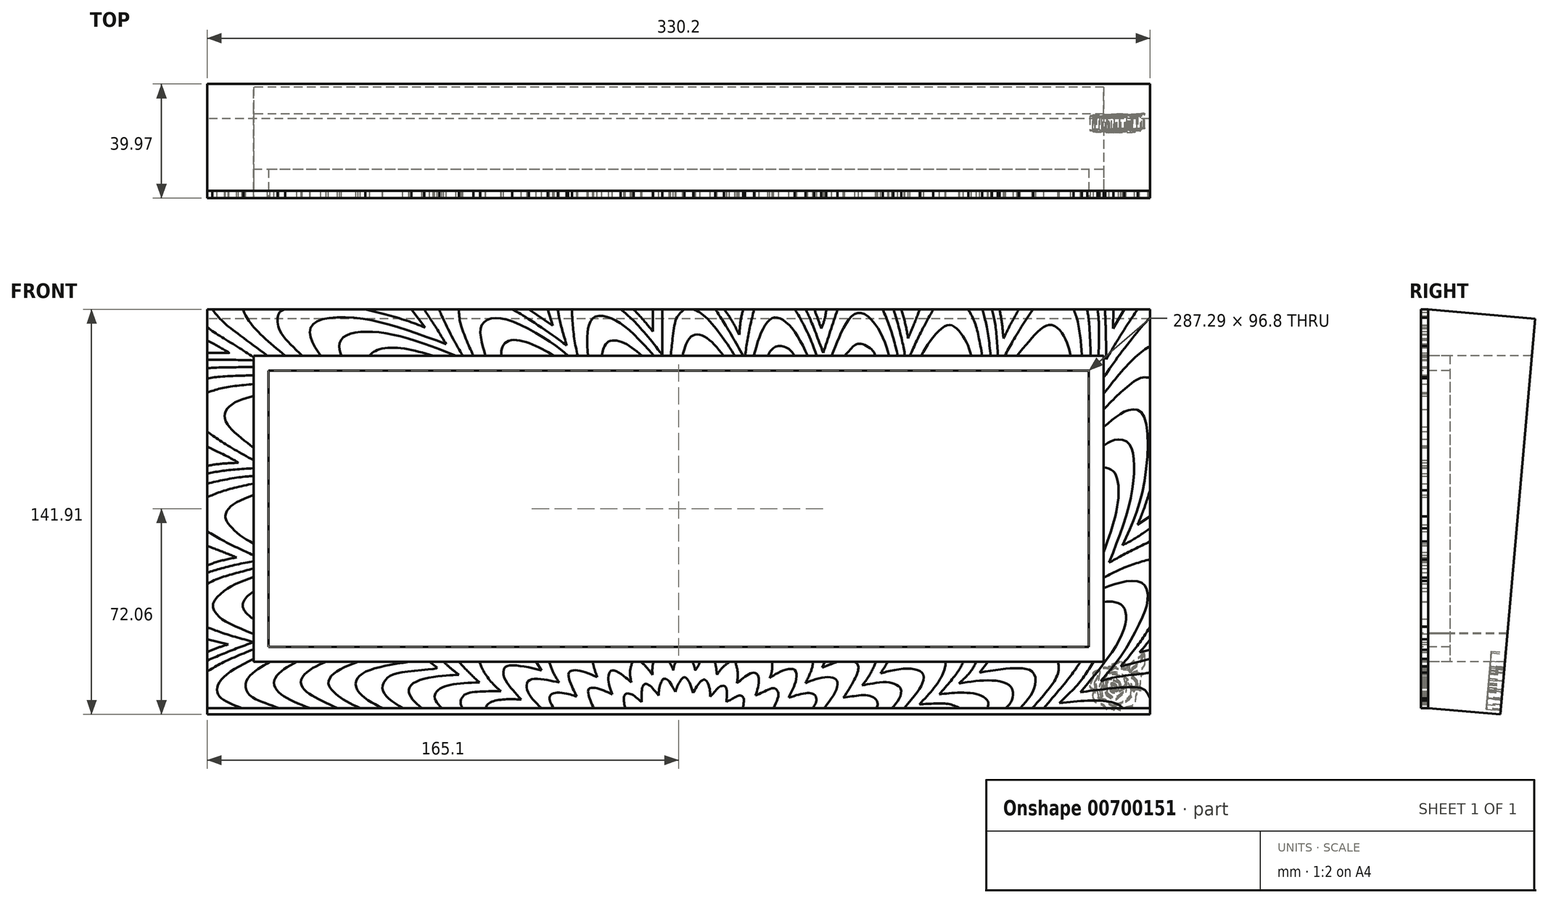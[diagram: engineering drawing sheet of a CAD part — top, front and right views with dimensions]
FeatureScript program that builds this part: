
annotation { "Feature Type Name" : "Feature", "Feature Type Description" : "" }
export const myFeature = defineFeature(function(context is Context, id is Id, definition is map)
    precondition{}
    {
        {
            var Q0;
            Q0=qCreatedBy(makeId("Front.planeOp"),FACE);
            var sketch = newSketch(context, id + "F0", { "sketchPlane" : qUnion([Q0])});
            skLineSegment(sketch, "E0.bottom", {"start": v(-143.64, 48.4) * mm, "end": v(143.64, 48.4) * mm});
            skLineSegment(sketch, "E0.top", {"start": v(-143.64, -48.4) * mm, "end": v(143.64, -48.4) * mm});
            skLineSegment(sketch, "E0.left", {"start": v(-143.64, 48.4) * mm, "end": v(-143.64, -48.4) * mm});
            skLineSegment(sketch, "E0.right", {"start": v(143.64, 48.4) * mm, "end": v(143.64, -48.4) * mm});
            skPoint(sketch, "E0.middle", {"position": v(0, 0) * mm});
            skLineSegment(sketch, "E1.bottom", {"start": v(-148.88, 53.63) * mm, "end": v(148.88, 53.63) * mm});
            skLineSegment(sketch, "E1.top", {"start": v(-148.88, -53.63) * mm, "end": v(148.88, -53.63) * mm});
            skLineSegment(sketch, "E1.left", {"start": v(-148.88, 53.63) * mm, "end": v(-148.88, -53.63) * mm});
            skLineSegment(sketch, "E1.right", {"start": v(148.88, 53.63) * mm, "end": v(148.88, -53.63) * mm});
            skLineSegment(sketch, "E2.bottom", {"start": v(-165.1, 69.85) * mm, "end": v(165.1, 69.85) * mm});
            skLineSegment(sketch, "E2.top", {"start": v(-165.1, -69.85) * mm, "end": v(165.1, -69.85) * mm});
            skLineSegment(sketch, "E2.left", {"start": v(-165.1, 69.85) * mm, "end": v(-165.1, -69.85) * mm});
            skLineSegment(sketch, "E2.right", {"start": v(165.1, 69.85) * mm, "end": v(165.1, -69.85) * mm});
            skFitSpline(sketch, "E3", {"points": [v(-148.88, -23.84) * mm, v(-155.66, -26.64) * mm, v(-160.5, -29.85) * mm, v(-163.16, -33.94) * mm, v(-161.11, -37.69) * mm, v(-156.13, -40.76) * mm, v(-148.88, -43.76) * mm, v(-148.88, -43.62) * mm], "startDerivative": vector(-39.33, -14.78) * mm, "endDerivative": vector(-2.7, 6.96) * mm});
            skFitSpline(sketch, "E4", {"points": [v(-148.88, -38.64) * mm, v(-150.68, -37.28) * mm, v(-152.18, -35.5) * mm, v(-152.66, -33.46) * mm, v(-151.36, -31) * mm, v(-148.88, -28.96) * mm], "startDerivative": vector(-9.73, 6.78) * mm, "endDerivative": vector(11.74, 8.3) * mm});
            skFitSpline(sketch, "E5", {"points": [v(-165.1, -26.23) * mm, v(-160.64, -24.25) * mm, v(-155.04, -22.55) * mm, v(-148.88, -20.91) * mm], "startDerivative": vector(13.98, 6.72) * mm, "endDerivative": vector(17.57, 4.62) * mm});
            skFitSpline(sketch, "E6", {"points": [v(-165.1, -22.41) * mm, v(-160.77, -21.05) * mm, v(-154.77, -19.55) * mm, v(-148.88, -18.39) * mm], "startDerivative": vector(13.7, 4.53) * mm, "endDerivative": vector(16.8, 3.12) * mm});
            skFitSpline(sketch, "E7", {"points": [v(-165.1, -19.82) * mm, v(-160.9, -18.39) * mm, v(-154.84, -17.03) * mm], "startDerivative": vector(8.7, 3.27) * mm, "endDerivative": vector(11.74, 2.35) * mm});
            skFitSpline(sketch, "E8", {"points": [v(-154.84, -17.03) * mm, v(-160.09, -14.91) * mm, v(-165.1, -13) * mm], "startDerivative": vector(-10.41, 4.25) * mm, "endDerivative": vector(-10.1, 3.8) * mm});
            skFitSpline(sketch, "E9", {"points": [v(-148.88, -16.28) * mm, v(-154.16, -13.82) * mm, v(-160.43, -10.68) * mm, v(-165.1, -7.96) * mm], "startDerivative": vector(-15.64, 7.2) * mm, "endDerivative": vector(-14.08, 8.56) * mm});
            skFitSpline(sketch, "E10", {"points": [v(-148.88, -12.18) * mm, v(-153.82, -9.12) * mm, v(-156.96, -6.11) * mm, v(-158.38, -4.14) * mm, v(-158.73, -2.7) * mm, v(-158.18, -0.73) * mm, v(-155.59, 1.8) * mm, v(-148.88, 4.86) * mm], "startDerivative": vector(-28.84, 16.16) * mm, "endDerivative": vector(36.5, 14.37) * mm});
            skFitSpline(sketch, "E11", {"points": [v(-165.1, 4.05) * mm, v(-159.27, 6.3) * mm, v(-148.88, 8.82) * mm], "startDerivative": vector(12.4, 5.36) * mm, "endDerivative": vector(19.72, 4.24) * mm});
            skFitSpline(sketch, "E12", {"points": [v(-165.1, 8.82) * mm, v(-158.25, 10.32) * mm, v(-151.7, 11.27) * mm, v(-148.88, 11.48) * mm], "startDerivative": vector(17.44, 4.14) * mm, "endDerivative": vector(10.33, 0.54) * mm});
            skFitSpline(sketch, "E13", {"points": [v(-165.1, 12.37) * mm, v(-158.93, 13.39) * mm, v(-148.88, 14.2) * mm], "startDerivative": vector(13.13, 2.51) * mm, "endDerivative": vector(19.08, 1.22) * mm});
            skFitSpline(sketch, "E14", {"points": [v(-165.1, 15.1) * mm, v(-160.09, 15.77) * mm, v(-154.23, 16.12) * mm], "startDerivative": vector(10.2, 1.6) * mm, "endDerivative": vector(11.54, 0.46) * mm});
            skFitSpline(sketch, "E15", {"points": [v(-165.1, 21.78) * mm, v(-161.73, 20.14) * mm, v(-156.4, 17.48) * mm, v(-154.23, 16.12) * mm], "startDerivative": vector(9.43, -4.6) * mm, "endDerivative": vector(6.91, -4.68) * mm});
            skFitSpline(sketch, "E16", {"points": [v(-165.1, 27.1) * mm, v(-161.73, 24.64) * mm, v(-156.27, 21.16) * mm, v(-148.88, 17) * mm], "startDerivative": vector(11.67, -8.74) * mm, "endDerivative": vector(19.59, -10.74) * mm});
            skFitSpline(sketch, "E17", {"points": [v(-148.88, 21.37) * mm, v(-153.68, 25.19) * mm, v(-157.9, 29.41) * mm, v(-159, 32.48) * mm, v(-158.25, 34.87) * mm, v(-154.43, 37.73) * mm, v(-148.88, 39.44) * mm], "startDerivative": vector(-24.8, 19.26) * mm, "endDerivative": vector(30.57, 7.1) * mm});
            skFitSpline(sketch, "E18", {"points": [v(-165.1, 40.73) * mm, v(-159.07, 42.44) * mm, v(-148.88, 43.67) * mm], "startDerivative": vector(12.79, 4.26) * mm, "endDerivative": vector(19.4, 1.7) * mm});
            skFitSpline(sketch, "E19", {"points": [v(-165.1, 45.64) * mm, v(-160.02, 46.32) * mm, v(-151.97, 46.67) * mm, v(-148.88, 46.8) * mm], "startDerivative": vector(13.86, 2.35) * mm, "endDerivative": vector(10.3, 0.54) * mm});
            skFitSpline(sketch, "E20", {"points": [v(-165.1, 49.26) * mm, v(-161.52, 49.46) * mm, v(-153.48, 49.6) * mm, v(-148.88, 49.6) * mm], "startDerivative": vector(11.27, 0.81) * mm, "endDerivative": vector(13.17, -0.05) * mm});
            skFitSpline(sketch, "E21", {"points": [v(-165.1, 52.19) * mm, v(-158.25, 52.19) * mm, v(-148.88, 51.98) * mm], "startDerivative": vector(14.29, 0.09) * mm, "endDerivative": vector(18.06, -0.48) * mm});
            skFitSpline(sketch, "E22", {"points": [v(-148.88, 53.08) * mm, v(-154.43, 56.69) * mm, v(-160.7, 60.58) * mm, v(-165.1, 63.5) * mm], "startDerivative": vector(-15.86, 10.52) * mm, "endDerivative": vector(-13.7, 9.38) * mm});
            skFitSpline(sketch, "E23", {"points": [v(-165.1, 59) * mm, v(-157.43, 54.58) * mm, v(-157.57, 54.58) * mm], "startDerivative": vector(13, -7.2) * mm, "endDerivative": vector(-1.78, 0.27) * mm});
            skFitSpline(sketch, "E24", {"points": [v(-157.43, 54.58) * mm, v(-165.1, 54.58) * mm], "startDerivative": vector(-7.67, 0) * mm, "endDerivative": vector(-7.67, 0) * mm});
            skFitSpline(sketch, "E25", {"points": [v(-163.36, 69.85) * mm, v(-159.89, 65.83) * mm, v(-155.45, 62.15) * mm, v(-144.06, 53.63) * mm], "startDerivative": vector(12.55, -15.56) * mm, "endDerivative": vector(28.56, -21.28) * mm});
            skFitSpline(sketch, "E26", {"points": [v(-152.45, 69.85) * mm, v(-151.9, 68.15) * mm, v(-148.22, 62.96) * mm, v(-137.8, 53.63) * mm], "startDerivative": vector(2, -8.7) * mm, "endDerivative": vector(23.58, -19.42) * mm});
            skFitSpline(sketch, "E27", {"points": [v(-137.8, 69.85) * mm, v(-139.63, 68.96) * mm, v(-140.45, 66.78) * mm, v(-139.7, 62.49) * mm, v(-131.86, 53.63) * mm], "startDerivative": vector(-12.3, -3.75) * mm, "endDerivative": vector(24.12, -22.95) * mm});
            skFitSpline(sketch, "E28", {"points": [v(-125.31, 53.63) * mm, v(-127.84, 57.5) * mm, v(-129.2, 61.94) * mm, v(-128.04, 64.67) * mm, v(-122.93, 66.78) * mm, v(-111.06, 66.58) * mm, v(-97.97, 63.5) * mm, v(-81.46, 57.71) * mm], "startDerivative": vector(-24.33, 33.6) * mm, "endDerivative": vector(79.98, -29.52) * mm});
            skFitSpline(sketch, "E29", {"points": [v(-89.17, 69.85) * mm, v(-85.42, 64.2) * mm, v(-81.46, 57.71) * mm], "startDerivative": vector(7.72, -11.4) * mm, "endDerivative": vector(7.7, -12.85) * mm});
            skFitSpline(sketch, "E30", {"points": [v(-109.76, 69.85) * mm, v(-97.63, 66.65) * mm, v(-88.76, 63.5) * mm], "startDerivative": vector(23.6, -5.77) * mm, "endDerivative": vector(18.29, -6.94) * mm});
            skFitSpline(sketch, "E31", {"points": [v(-88.76, 63.5) * mm, v(-93.6, 69.85) * mm], "startDerivative": vector(-4.84, 6.34) * mm, "endDerivative": vector(-4.84, 6.34) * mm});
            skFitSpline(sketch, "E32", {"points": [v(-118.15, 53.63) * mm, v(-118.9, 56.76) * mm, v(-117.67, 59.83) * mm, v(-111.95, 61.87) * mm, v(-98.72, 60.71) * mm, v(-77.99, 53.63) * mm], "startDerivative": vector(-8.96, 24.79) * mm, "endDerivative": vector(66.04, -25.79) * mm});
            skFitSpline(sketch, "E33", {"points": [v(-108.2, 53.63) * mm, v(-107.38, 54.58) * mm, v(-104.24, 56) * mm, v(-96.47, 56.14) * mm, v(-85.97, 53.63) * mm], "startDerivative": vector(5.26, 7.61) * mm, "endDerivative": vector(29.33, -8.5) * mm});
            skFitSpline(sketch, "E34", {"points": [v(-75.6, 53.63) * mm, v(-79.35, 60.24) * mm, v(-82.83, 67.33) * mm, v(-83.85, 69.85) * mm], "startDerivative": vector(-9.68, 16.45) * mm, "endDerivative": vector(-3.62, 9.55) * mm});
            skFitSpline(sketch, "E35", {"points": [v(-71.92, 53.63) * mm, v(-74.65, 59.9) * mm, v(-76.62, 65.9) * mm, v(-76.96, 69.85) * mm], "startDerivative": vector(-7.6, 16.87) * mm, "endDerivative": vector(-0.28, 13.46) * mm});
            skFitSpline(sketch, "E36", {"points": [v(-67.7, 53.63) * mm, v(-68.92, 58.33) * mm, v(-69.4, 62.76) * mm, v(-68.03, 65.49) * mm, v(-64.55, 66.78) * mm, v(-56.92, 65.08) * mm, v(-43.82, 57.71) * mm, v(-38.78, 53.63) * mm], "startDerivative": vector(-10.07, 36.36) * mm, "endDerivative": vector(28.31, -25.37) * mm});
            skFitSpline(sketch, "E37", {"points": [v(-62.17, 53.63) * mm, v(-61.83, 56.42) * mm, v(-60.05, 58.6) * mm, v(-56.03, 59) * mm, v(-49.82, 56.96) * mm, v(-43.62, 53.63) * mm], "startDerivative": vector(0.32, 18.02) * mm, "endDerivative": vector(24.27, -14) * mm});
            skFitSpline(sketch, "E38", {"points": [v(-58.28, 69.85) * mm, v(-53.03, 66.78) * mm, v(-39.19, 57.1) * mm, v(-39.32, 57.1) * mm], "startDerivative": vector(10.3, -5.3) * mm, "endDerivative": vector(-3.94, 0.9) * mm});
            skFitSpline(sketch, "E39", {"points": [v(-52.48, 69.85) * mm, v(-44.1, 64.12) * mm], "startDerivative": vector(8.39, -5.73) * mm, "endDerivative": vector(8.39, -5.73) * mm});
            skFitSpline(sketch, "E40", {"points": [v(-44.1, 64.12) * mm, v(-45.87, 69.85) * mm], "startDerivative": vector(-1.77, 5.73) * mm, "endDerivative": vector(-1.77, 5.73) * mm});
            skFitSpline(sketch, "E41", {"points": [v(-42.32, 69.85) * mm, v(-41.7, 66.24) * mm, v(-39.19, 57.1) * mm], "startDerivative": vector(1.12, -8.4) * mm, "endDerivative": vector(4.86, -16.48) * mm});
            skFitSpline(sketch, "E42", {"points": [v(-35.37, 53.63) * mm, v(-36.6, 59.9) * mm, v(-37.2, 66.24) * mm, v(-37.41, 69.85) * mm], "startDerivative": vector(-3.76, 16.86) * mm, "endDerivative": vector(-0.63, 12.2) * mm});
            skFitSpline(sketch, "E43", {"points": [v(-31.75, 53.63) * mm, v(-32.03, 59.9) * mm, v(-31.28, 64.67) * mm, v(-29.23, 67.33) * mm, v(-24.6, 67.05) * mm, v(-18.39, 63.5) * mm, v(-8.7, 53.63) * mm], "startDerivative": vector(-2.92, 38.7) * mm, "endDerivative": vector(40.7, -45.2) * mm});
            skFitSpline(sketch, "E44", {"points": [v(-26.91, 53.63) * mm, v(-26.37, 56.14) * mm, v(-24.53, 58.53) * mm, v(-19.96, 58.46) * mm, v(-12.8, 53.63) * mm], "startDerivative": vector(1.83, 13.08) * mm, "endDerivative": vector(20.6, -17.01) * mm});
            skFitSpline(sketch, "E45", {"points": [v(-20.3, 69.85) * mm, v(-15.05, 65.15) * mm, v(-5.74, 53.97) * mm], "startDerivative": vector(12.18, -9.92) * mm, "endDerivative": vector(16.67, -21.17) * mm});
            skFitSpline(sketch, "E46", {"points": [v(-5.74, 53.97) * mm, v(-5.74, 60.07) * mm, v(-5.74, 67.58) * mm, v(-5.74, 69.85) * mm], "startDerivative": vector(0, 15.42) * mm, "endDerivative": vector(0, 8.42) * mm});
            skFitSpline(sketch, "E47", {"points": [v(-15.8, 69.85) * mm, v(-12.11, 65.88) * mm, v(-9.05, 62.06) * mm], "startDerivative": vector(7.41, -7.73) * mm, "endDerivative": vector(6.08, -7.85) * mm});
            skFitSpline(sketch, "E48", {"points": [v(-9.05, 62.06) * mm, v(-9.05, 69.85) * mm], "startDerivative": vector(0, 7.8) * mm, "endDerivative": vector(0, 7.8) * mm});
            skFitSpline(sketch, "E49", {"points": [v(-2.77, 53.63) * mm, v(-2.16, 59.4) * mm, v(-0.66, 66.9) * mm, v(2, 69.85) * mm], "startDerivative": vector(1.72, 15.96) * mm, "endDerivative": vector(10.73, 8.47) * mm});
            skFitSpline(sketch, "E50", {"points": [v(5.14, 69.85) * mm, v(8.34, 68.13) * mm, v(15.1, 60.42) * mm, v(19.66, 53.63) * mm], "startDerivative": vector(12.47, -4.75) * mm, "endDerivative": vector(11.4, -17.9) * mm});
            skFitSpline(sketch, "E51", {"points": [v(1.39, 53.63) * mm, v(2.55, 57.56) * mm, v(5.14, 60.76) * mm, v(9.43, 60.08) * mm, v(15.78, 53.63) * mm], "startDerivative": vector(4.01, 17.68) * mm, "endDerivative": vector(18.96, -23.43) * mm});
            skFitSpline(sketch, "E52", {"points": [v(12.84, 69.85) * mm, v(16.46, 64.24) * mm, v(22.6, 53.63) * mm], "startDerivative": vector(8.06, -12.1) * mm, "endDerivative": vector(11.28, -19.95) * mm});
            skFitSpline(sketch, "E53", {"points": [v(15.84, 69.85) * mm, v(18.03, 66.9) * mm, v(21.23, 60.97) * mm], "startDerivative": vector(5.05, -6.24) * mm, "endDerivative": vector(5.7, -11.28) * mm});
            skFitSpline(sketch, "E54", {"points": [v(21.23, 60.97) * mm, v(21.78, 66.22) * mm, v(22.6, 69.85) * mm], "startDerivative": vector(0.79, 10.12) * mm, "endDerivative": vector(1.97, 7.57) * mm});
            skFitSpline(sketch, "E55", {"points": [v(23.25, 53.63) * mm, v(24.5, 61.49) * mm, v(26.41, 69.85) * mm], "startDerivative": vector(2.24, 15.93) * mm, "endDerivative": vector(4.07, 16.52) * mm});
            skFitSpline(sketch, "E56", {"points": [v(26.35, 53.63) * mm, v(28.6, 60.97) * mm, v(31.4, 65.74) * mm, v(33.78, 67.04) * mm, v(36.5, 66.15) * mm, v(40.6, 62.06) * mm, v(45.23, 53.63) * mm], "startDerivative": vector(10.1, 38.33) * mm, "endDerivative": vector(19.94, -41.1) * mm});
            skFitSpline(sketch, "E57", {"points": [v(31.19, 53.63) * mm, v(33.03, 56.2) * mm, v(35.48, 57.08) * mm, v(38.69, 55.85) * mm, v(40.6, 53.63) * mm], "startDerivative": vector(6.45, 11.28) * mm, "endDerivative": vector(6.6, -9.69) * mm});
            skFitSpline(sketch, "E58", {"points": [v(40.67, 69.85) * mm, v(42.64, 66.63) * mm, v(46.33, 58.99) * mm, v(48.37, 53.63) * mm], "startDerivative": vector(6.8, -10.33) * mm, "endDerivative": vector(5.33, -15.03) * mm});
            skFitSpline(sketch, "E59", {"points": [v(44.48, 69.85) * mm, v(46.33, 65.8) * mm, v(50.62, 54.62) * mm], "startDerivative": vector(4.48, -9.3) * mm, "endDerivative": vector(7.55, -20.27) * mm});
            skFitSpline(sketch, "E60", {"points": [v(50.62, 54.62) * mm, v(53.08, 62.06) * mm, v(55.67, 69.85) * mm], "startDerivative": vector(4.93, 14.96) * mm, "endDerivative": vector(5.16, 15.5) * mm});
            skFitSpline(sketch, "E61", {"points": [v(47.49, 69.85) * mm, v(48.71, 66.63) * mm, v(49.94, 63.08) * mm], "startDerivative": vector(2.53, -6.5) * mm, "endDerivative": vector(2.38, -7.04) * mm});
            skFitSpline(sketch, "E62", {"points": [v(49.94, 63.08) * mm, v(51.17, 66.63) * mm, v(51.71, 69.85) * mm], "startDerivative": vector(2.7, 6.9) * mm, "endDerivative": vector(0.83, 6.63) * mm});
            skFitSpline(sketch, "E63", {"points": [v(53.55, 53.63) * mm, v(56.28, 60.22) * mm, v(59.83, 66.63) * mm, v(63.1, 68.68) * mm, v(67.2, 66.63) * mm, v(71.56, 59.94) * mm, v(73.67, 53.63) * mm], "startDerivative": vector(14.4, 36.04) * mm, "endDerivative": vector(9.88, -35.67) * mm});
            skFitSpline(sketch, "E64", {"points": [v(58.2, 53.63) * mm, v(61.26, 56.94) * mm, v(63.51, 57.83) * mm, v(67.53, 55.85) * mm, v(68.9, 53.63) * mm], "startDerivative": vector(11.09, 13.09) * mm, "endDerivative": vector(4.16, -10.31) * mm});
            skFitSpline(sketch, "E65", {"points": [v(71.49, 69.85) * mm, v(74.49, 62.06) * mm, v(76.74, 53.63) * mm], "startDerivative": vector(6.47, -15.53) * mm, "endDerivative": vector(4.04, -16.91) * mm});
            skFitSpline(sketch, "E66", {"points": [v(75.17, 69.85) * mm, v(76.53, 65.67) * mm, v(78.38, 58.3) * mm, v(79.26, 53.63) * mm], "startDerivative": vector(4.43, -12.65) * mm, "endDerivative": vector(2.4, -13.87) * mm});
            skFitSpline(sketch, "E67", {"points": [v(77.97, 69.85) * mm, v(79.33, 64.99) * mm, v(80.35, 59.67) * mm], "startDerivative": vector(2.96, -9.76) * mm, "endDerivative": vector(1.82, -10.6) * mm});
            skFitSpline(sketch, "E68", {"points": [v(80.35, 59.67) * mm, v(82.6, 65.13) * mm, v(84.44, 69.85) * mm], "startDerivative": vector(4.47, 10.7) * mm, "endDerivative": vector(3.7, 9.65) * mm});
            skFitSpline(sketch, "E69", {"points": [v(81.04, 53.63) * mm, v(84.38, 60.97) * mm, v(89.15, 69.85) * mm], "startDerivative": vector(6.61, 15.25) * mm, "endDerivative": vector(9.56, 17.17) * mm});
            skFitSpline(sketch, "E70", {"points": [v(85, 53.63) * mm, v(88.74, 59.67) * mm, v(93.17, 63.9) * mm, v(95.7, 64.24) * mm, v(98.36, 62.06) * mm, v(100.81, 58.3) * mm, v(102.52, 53.63) * mm], "startDerivative": vector(16.58, 30) * mm, "endDerivative": vector(8.73, -28.02) * mm});
            skFitSpline(sketch, "E71", {"points": [v(106.33, 69.85) * mm, v(107.7, 64.65) * mm, v(109.33, 53.63) * mm], "startDerivative": vector(3.44, -11.46) * mm, "endDerivative": vector(2.61, -20.45) * mm});
            skFitSpline(sketch, "E72", {"points": [v(109.68, 69.85) * mm, v(110.9, 64.44) * mm, v(111.79, 53.63) * mm], "startDerivative": vector(3.24, -11.8) * mm, "endDerivative": vector(1.1, -20.18) * mm});
            skFitSpline(sketch, "E73", {"points": [v(101.5, 69.85) * mm, v(103.47, 65.8) * mm, v(104.9, 60.97) * mm, v(106.33, 53.63) * mm], "startDerivative": vector(7.11, -13.3) * mm, "endDerivative": vector(3.64, -20.03) * mm});
            skFitSpline(sketch, "E74", {"points": [v(112.4, 69.85) * mm, v(113.15, 65.4) * mm, v(113.77, 59.67) * mm], "startDerivative": vector(1.7, -9.17) * mm, "endDerivative": vector(1.04, -11.15) * mm});
            skFitSpline(sketch, "E75", {"points": [v(113.77, 59.67) * mm, v(116.09, 64.3) * mm, v(119.09, 69.85) * mm], "startDerivative": vector(4.67, 9.55) * mm, "endDerivative": vector(5.94, 10.78) * mm});
            skFitSpline(sketch, "E76", {"points": [v(114.24, 53.63) * mm, v(118, 60.42) * mm, v(124.13, 69.85) * mm], "startDerivative": vector(7.6, 14.46) * mm, "endDerivative": vector(12.05, 17.89) * mm});
            skFitSpline(sketch, "E77", {"points": [v(118.47, 53.63) * mm, v(123.59, 59.67) * mm, v(127.88, 63.7) * mm, v(130.82, 64.3) * mm, v(133.88, 62.06) * mm, v(136.2, 57.62) * mm, v(137.23, 53.63) * mm], "startDerivative": vector(24.07, 29.06) * mm, "endDerivative": vector(5.32, -25.45) * mm});
            skFitSpline(sketch, "E78", {"points": [v(138.32, 69.85) * mm, v(139.48, 66.63) * mm, v(140.63, 60.28) * mm, v(141.25, 53.63) * mm], "startDerivative": vector(4.55, -10.98) * mm, "endDerivative": vector(1.33, -17.7) * mm});
            skFitSpline(sketch, "E79", {"points": [v(143.09, 69.85) * mm, v(143.7, 65.4) * mm, v(144.32, 53.63) * mm], "startDerivative": vector(1.73, -10.25) * mm, "endDerivative": vector(0.8, -21.32) * mm});
            skFitSpline(sketch, "E80", {"points": [v(146.7, 69.85) * mm, v(147.18, 64.65) * mm, v(147.04, 53.63) * mm], "startDerivative": vector(1.46, -11.56) * mm, "endDerivative": vector(-0.65, -20.34) * mm});
            skFitSpline(sketch, "E81", {"points": [v(149.3, 69.85) * mm, v(149.57, 63.08) * mm, v(149.77, 52.37) * mm], "startDerivative": vector(0.67, -14.4) * mm, "endDerivative": vector(0.3, -20.32) * mm});
            skFitSpline(sketch, "E82", {"points": [v(149.77, 52.37) * mm, v(155.57, 62.06) * mm, v(160.75, 69.85) * mm], "startDerivative": vector(11.13, 19.06) * mm, "endDerivative": vector(10.83, 15.84) * mm});
            skFitSpline(sketch, "E83", {"points": [v(152.16, 63.08) * mm, v(152.23, 69.85) * mm], "startDerivative": vector(0.07, 6.77) * mm, "endDerivative": vector(0.07, 6.77) * mm});
            skFitSpline(sketch, "E84", {"points": [v(152.16, 63.08) * mm, v(156.11, 69.85) * mm], "startDerivative": vector(3.96, 6.77) * mm, "endDerivative": vector(3.96, 6.77) * mm});
            skFitSpline(sketch, "E85", {"points": [v(148.88, 46.03) * mm, v(155.1, 54.9) * mm, v(162.66, 64.3) * mm, v(165.1, 66.97) * mm], "startDerivative": vector(15.04, 22.34) * mm, "endDerivative": vector(9.51, 9.94) * mm});
            skFitSpline(sketch, "E86", {"points": [v(148.88, 40.3) * mm, v(154.68, 47.53) * mm, v(161.43, 54.42) * mm, v(165.1, 57.01) * mm], "startDerivative": vector(14.89, 19.32) * mm, "endDerivative": vector(13.38, 8.38) * mm});
            skFitSpline(sketch, "E87", {"points": [v(148.88, 34.85) * mm, v(153.11, 39.15) * mm, v(157.48, 43.03) * mm, v(162.25, 45.96) * mm, v(165.1, 45.76) * mm], "startDerivative": vector(15.42, 15.98) * mm, "endDerivative": vector(14.28, -3.64) * mm});
            skFitSpline(sketch, "E88", {"points": [v(148.88, 28.72) * mm, v(153.89, 32.66) * mm, v(158.66, 34.8) * mm, v(162.72, 32.9) * mm, v(162.72, 7.48) * mm, v(155.44, -12.8) * mm], "startDerivative": vector(32.62, 27.37) * mm, "endDerivative": vector(-29.95, -63.67) * mm});
            skFitSpline(sketch, "E89", {"points": [v(155.44, -12.8) * mm, v(159.98, -10.3) * mm, v(165.1, -6.84) * mm], "startDerivative": vector(9.41, 4.91) * mm, "endDerivative": vector(9.9, 6.99) * mm});
            skFitSpline(sketch, "E90", {"points": [v(160.7, -5.65) * mm, v(165.1, -2.66) * mm], "startDerivative": vector(4.4, 2.98) * mm, "endDerivative": vector(4.4, 2.98) * mm});
            skFitSpline(sketch, "E91", {"points": [v(160.7, -5.65) * mm, v(162.96, 0) * mm, v(165.1, 6.52) * mm], "startDerivative": vector(4.8, 11.4) * mm, "endDerivative": vector(4.02, 12.93) * mm});
            skFitSpline(sketch, "E92", {"points": [v(150.8, -18.85) * mm, v(156.66, -15.65) * mm, v(165.1, -11.49) * mm], "startDerivative": vector(12.2, 6.86) * mm, "endDerivative": vector(16.3, 7.84) * mm});
            skFitSpline(sketch, "E93", {"points": [v(148.88, 14.47) * mm, v(151.98, 13.4) * mm, v(153.89, 8.86) * mm, v(153.3, -0.93) * mm, v(148.88, -15.25) * mm], "startDerivative": vector(20.66, -3.26) * mm, "endDerivative": vector(-14.87, -42) * mm});
            skFitSpline(sketch, "E94", {"points": [v(148.88, -24.07) * mm, v(157.48, -20.05) * mm, v(165.1, -17.73) * mm], "startDerivative": vector(16.62, 8.45) * mm, "endDerivative": vector(15.82, 4.17) * mm});
            skFitSpline(sketch, "E95", {"points": [v(148.88, -27.82) * mm, v(154.68, -25.84) * mm, v(160.7, -25.36) * mm, v(163.55, -27.34) * mm, v(164.23, -31.98) * mm, v(162.39, -38.05) * mm, v(155.44, -50.8) * mm, v(147.77, -60.35) * mm], "startDerivative": vector(42.5, 16.57) * mm, "endDerivative": vector(-41.64, -46.77) * mm});
            skFitSpline(sketch, "E96", {"points": [v(148.88, -32.67) * mm, v(151.95, -32.55) * mm, v(155.05, -33.62) * mm, v(156.6, -36.49) * mm, v(154.81, -44.96) * mm, v(140.73, -64.3) * mm], "startDerivative": vector(22.67, 2.49) * mm, "endDerivative": vector(-46.2, -55.37) * mm});
            skFitSpline(sketch, "E97", {"points": [v(140.73, -64.3) * mm, v(147.65, -63.34) * mm, v(157.44, -62.5) * mm, v(163.04, -63.34) * mm, v(165.1, -66.44) * mm], "startDerivative": vector(24.84, 3.68) * mm, "endDerivative": vector(8.15, -18.92) * mm});
            skFitSpline(sketch, "E98", {"points": [v(147.77, -60.35) * mm, v(153.5, -58.92) * mm, v(162.8, -57.73) * mm, v(165.1, -57.37) * mm], "startDerivative": vector(14.5, 4.39) * mm, "endDerivative": vector(8.35, 1.52) * mm});
            skFitSpline(sketch, "E99", {"points": [v(154.81, -55.22) * mm, v(161.37, -46.99) * mm, v(165.1, -41.26) * mm], "startDerivative": vector(12.82, 15.43) * mm, "endDerivative": vector(7.57, 12.39) * mm});
            skFitSpline(sketch, "E100", {"points": [v(154.81, -55.22) * mm, v(165.1, -52.6) * mm], "startDerivative": vector(10.29, 2.63) * mm, "endDerivative": vector(10.29, 2.63) * mm});
            skFitSpline(sketch, "E101", {"points": [v(161.37, -50.33) * mm, v(165.1, -45.68) * mm, v(165.1, -45.56) * mm], "startDerivative": vector(6.12, 7.22) * mm, "endDerivative": vector(-0.26, 0.7) * mm});
            skFitSpline(sketch, "E102", {"points": [v(161.37, -50.33) * mm, v(165.1, -49.38) * mm], "startDerivative": vector(3.73, 0.95) * mm, "endDerivative": vector(3.73, 0.95) * mm});
            skFitSpline(sketch, "E103", {"points": [v(133.33, -68.11) * mm, v(140.73, -60.35) * mm, v(145.26, -53.63) * mm], "startDerivative": vector(14.93, 14.52) * mm, "endDerivative": vector(8.8, 14.45) * mm});
            skFitSpline(sketch, "E104", {"points": [v(133.33, -68.11) * mm, v(145.5, -67.16) * mm, v(152.9, -68.11) * mm, v(155.65, -69.85) * mm], "startDerivative": vector(28.97, 3.25) * mm, "endDerivative": vector(10.49, -8.56) * mm});
            skFitSpline(sketch, "E105", {"points": [v(140.73, -53.63) * mm, v(137.27, -58.56) * mm, v(127.84, -69.85) * mm], "startDerivative": vector(-7.58, -11.5) * mm, "endDerivative": vector(-17.48, -20.3) * mm});
            skFitSpline(sketch, "E106", {"points": [v(132.81, -53.63) * mm, v(133.08, -54.75) * mm, v(132.81, -57.67) * mm, v(130.51, -61.88) * mm, v(123.85, -69.85) * mm], "startDerivative": vector(2.51, -7.5) * mm, "endDerivative": vector(-19, -21.7) * mm});
            skFitSpline(sketch, "E107", {"points": [v(119.68, -69.85) * mm, v(123.19, -65.54) * mm, v(124.98, -60.98) * mm, v(124, -57.2) * mm, v(120.3, -55.92) * mm, v(114.46, -56.07) * mm, v(105.42, -57.36) * mm], "startDerivative": vector(22.35, 24.78) * mm, "endDerivative": vector(-43.85, -6.97) * mm});
            skFitSpline(sketch, "E108", {"points": [v(105.42, -57.36) * mm, v(108.26, -53.63) * mm], "startDerivative": vector(2.84, 3.74) * mm, "endDerivative": vector(2.84, 3.74) * mm});
            skFitSpline(sketch, "E109", {"points": [v(114.6, -69.85) * mm, v(116.87, -66.57) * mm, v(116.27, -62.27) * mm, v(109, -60.12) * mm, v(98.13, -61.2) * mm], "startDerivative": vector(13.91, 14.94) * mm, "endDerivative": vector(-33.46, -5.33) * mm});
            skFitSpline(sketch, "E110", {"points": [v(98.13, -61.2) * mm, v(102.07, -57.26) * mm, v(104.22, -53.63) * mm], "startDerivative": vector(8.1, 7.25) * mm, "endDerivative": vector(3.98, 7.9) * mm});
            skFitSpline(sketch, "E111", {"points": [v(99.74, -53.63) * mm, v(97.7, -57.18) * mm, v(91.29, -65.02) * mm], "startDerivative": vector(-4.24, -8.42) * mm, "endDerivative": vector(-12.09, -13.96) * mm});
            skFitSpline(sketch, "E112", {"points": [v(91.29, -65.02) * mm, v(96.74, -64.48) * mm, v(104.72, -65.02) * mm, v(108.27, -67.34) * mm, v(108.2, -69.85) * mm], "startDerivative": vector(19.06, 2.44) * mm, "endDerivative": vector(-3.42, -14.51) * mm});
            skFitSpline(sketch, "E113", {"points": [v(-165.1, -41.5) * mm, v(-158.73, -43.82) * mm, v(-148.88, -46.69) * mm], "startDerivative": vector(13.4, -5.16) * mm, "endDerivative": vector(18.87, -5.2) * mm});
            skFitSpline(sketch, "E114", {"points": [v(-148.88, -46.69) * mm, v(-157.84, -50.1) * mm, v(-165.1, -53.17) * mm], "startDerivative": vector(-17.57, -6.51) * mm, "endDerivative": vector(-14.84, -6.44) * mm});
            skFitSpline(sketch, "E115", {"points": [v(-165.1, -50.17) * mm, v(-161.52, -48.73) * mm, v(-157.77, -47.5) * mm], "startDerivative": vector(7.14, 3) * mm, "endDerivative": vector(7.52, 2.33) * mm});
            skFitSpline(sketch, "E116", {"points": [v(-157.77, -47.5) * mm, v(-165.1, -45.67) * mm], "startDerivative": vector(-7.33, 1.84) * mm, "endDerivative": vector(-7.33, 1.84) * mm});
            skFitSpline(sketch, "E117", {"points": [v(-165.1, -57.02) * mm, v(-159.4, -53.75) * mm, v(-148.88, -49.25) * mm], "startDerivative": vector(12.07, 7.53) * mm, "endDerivative": vector(20.01, 8) * mm});
            skFitSpline(sketch, "E118", {"points": [v(-152.93, -69.85) * mm, v(-158.38, -67.52) * mm, v(-161.04, -65.4) * mm, v(-161.59, -62.68) * mm, v(-159.27, -58.86) * mm, v(-148.88, -52.52) * mm], "startDerivative": vector(-27.82, 10.81) * mm, "endDerivative": vector(40.24, 20.96) * mm});
            skFitSpline(sketch, "E119", {"points": [v(-143.08, -53.63) * mm, v(-148.2, -56.73) * mm, v(-151.47, -60.68) * mm, v(-150.72, -64.77) * mm, v(-145.67, -67.7) * mm, v(-140.01, -69.85) * mm], "startDerivative": vector(-25.14, -13.6) * mm, "endDerivative": vector(26.24, -9.8) * mm});
            skFitSpline(sketch, "E120", {"points": [v(-129.1, -69.85) * mm, v(-137.08, -66.41) * mm, v(-140.97, -63.2) * mm, v(-141.65, -60.2) * mm, v(-139.13, -56.86) * mm, v(-133.74, -53.63) * mm], "startDerivative": vector(-33.5, 12.8) * mm, "endDerivative": vector(26.5, 13.83) * mm});
            skFitSpline(sketch, "E121", {"points": [v(-119.49, -69.85) * mm, v(-126.85, -66.27) * mm, v(-131.15, -63.34) * mm, v(-132.24, -60.14) * mm, v(-129.17, -56.45) * mm, v(-123.5, -53.63) * mm], "startDerivative": vector(-31.61, 14.93) * mm, "endDerivative": vector(27.48, 11.44) * mm});
            skFitSpline(sketch, "E122", {"points": [v(-111.5, -69.85) * mm, v(-117.71, -66.62) * mm, v(-121.12, -63.82) * mm, v(-122.62, -61.23) * mm, v(-121.05, -57.95) * mm, v(-112.26, -53.63) * mm], "startDerivative": vector(-29.05, 13.8) * mm, "endDerivative": vector(38.22, 14.46) * mm});
            skFitSpline(sketch, "E123", {"points": [v(-103.67, -69.85) * mm, v(-109.74, -66.41) * mm, v(-112.87, -62.73) * mm, v(-112.53, -59.39) * mm, v(-107.48, -56.25) * mm, v(-94.32, -53.63) * mm], "startDerivative": vector(-31.26, 15.51) * mm, "endDerivative": vector(50.21, 7.5) * mm});
            skFitSpline(sketch, "E124", {"points": [v(-96.71, -69.85) * mm, v(-102.1, -65.93) * mm, v(-103.73, -62.6) * mm, v(-102.17, -59.39) * mm, v(-96.64, -57.27) * mm, v(-84.64, -55.77) * mm, v(-84.64, -55.64) * mm], "startDerivative": vector(-29.69, 18.55) * mm, "endDerivative": vector(-2.64, 4.68) * mm});
            skFitSpline(sketch, "E125", {"points": [v(-87.3, -53.63) * mm, v(-84.62, -55.68) * mm], "startDerivative": vector(2.69, -2.06) * mm, "endDerivative": vector(2.69, -2.06) * mm});
            skFitSpline(sketch, "E126", {"points": [v(-89.96, -69.85) * mm, v(-93.5, -66.34) * mm, v(-94.53, -63.34) * mm, v(-91.8, -60.48) * mm, v(-82.25, -58.5) * mm, v(-76.94, -58.16) * mm], "startDerivative": vector(-20.27, 17.49) * mm, "endDerivative": vector(23.28, 1.02) * mm});
            skFitSpline(sketch, "E127", {"points": [v(-82.25, -53.63) * mm, v(-80.07, -55.68) * mm, v(-76.94, -58.16) * mm], "startDerivative": vector(4.43, -4.39) * mm, "endDerivative": vector(6.16, -4.68) * mm});
            skFitSpline(sketch, "E128", {"points": [v(-83, -69.85) * mm, v(-85.4, -66.41) * mm, v(-84.62, -63.82) * mm, v(-80.07, -61.7) * mm, v(-69.77, -60.82) * mm], "startDerivative": vector(-14.25, 15.36) * mm, "endDerivative": vector(31.62, 1.13) * mm});
            skFitSpline(sketch, "E129", {"points": [v(-69.77, -60.82) * mm, v(-73.66, -57.14) * mm, v(-76.94, -53.63) * mm], "startDerivative": vector(-7.78, 7.16) * mm, "endDerivative": vector(-6.53, 7.23) * mm});
            skFitSpline(sketch, "E130", {"points": [v(-75.78, -69.85) * mm, v(-76.39, -67.77) * mm, v(-75.1, -65.25) * mm, v(-70.66, -64.1) * mm, v(-62.27, -63.89) * mm], "startDerivative": vector(-5.3, 10.97) * mm, "endDerivative": vector(25.06, 0.13) * mm});
            skFitSpline(sketch, "E131", {"points": [v(-62.27, -63.89) * mm, v(-66.02, -60.2) * mm, v(-68.96, -55.68) * mm, v(-69.77, -53.63) * mm], "startDerivative": vector(-10.24, 8.96) * mm, "endDerivative": vector(-2.56, 7.6) * mm});
            skFitSpline(sketch, "E132", {"points": [v(-67.52, -69.85) * mm, v(-66.7, -68.32) * mm, v(-62.27, -66.89) * mm, v(-55.18, -66.82) * mm], "startDerivative": vector(2.2, 7.57) * mm, "endDerivative": vector(16.65, -0.72) * mm});
            skFitSpline(sketch, "E133", {"points": [v(-55.18, -66.82) * mm, v(-58.46, -63.07) * mm, v(-61.05, -59.18) * mm, v(-60.91, -55.68) * mm, v(-57.02, -54.89) * mm, v(-48.02, -56.6) * mm], "startDerivative": vector(-16.64, 18.95) * mm, "endDerivative": vector(35.67, -8.36) * mm});
            skFitSpline(sketch, "E134", {"points": [v(-48.02, -56.6) * mm, v(-49.86, -53.63) * mm], "startDerivative": vector(-1.84, 2.97) * mm, "endDerivative": vector(-1.84, 2.97) * mm});
            skFitSpline(sketch, "E135", {"points": [v(-48.02, -69.85) * mm, v(-51.98, -65.6) * mm, v(-53.27, -62.18) * mm, v(-52.32, -60.07) * mm, v(-47.54, -59.8) * mm, v(-41.82, -60.82) * mm], "startDerivative": vector(-19.24, 18.25) * mm, "endDerivative": vector(24.17, -4.98) * mm});
            skFitSpline(sketch, "E136", {"points": [v(-41.82, -60.82) * mm, v(-43.8, -57.61) * mm, v(-45.36, -53.63) * mm], "startDerivative": vector(-4.34, 6.36) * mm, "endDerivative": vector(-2.77, 8.01) * mm});
            skFitSpline(sketch, "E137", {"points": [v(-43.68, -69.85) * mm, v(-45.23, -66.82) * mm, v(-44.34, -64.84) * mm, v(-39.23, -64.77) * mm, v(-35.68, -65.8) * mm], "startDerivative": vector(-8.62, 12.43) * mm, "endDerivative": vector(12.26, -4.3) * mm});
            skFitSpline(sketch, "E138", {"points": [v(-35.68, -65.8) * mm, v(-37.66, -61.57) * mm, v(-38.4, -57.4) * mm, v(-35.68, -56.6) * mm, v(-28.52, -58.98) * mm], "startDerivative": vector(-8, 15.9) * mm, "endDerivative": vector(24.07, -10.26) * mm});
            skFitSpline(sketch, "E139", {"points": [v(-28.52, -58.98) * mm, v(-29.61, -55.68) * mm, v(-30.09, -53.63) * mm], "startDerivative": vector(-2.18, 6.2) * mm, "endDerivative": vector(-0.9, 4.44) * mm});
            skFitSpline(sketch, "E140", {"points": [v(-29.75, -69.85) * mm, v(-31.38, -65.8) * mm, v(-31.45, -63.07) * mm, v(-28.52, -62.93) * mm, v(-23.27, -64.98) * mm], "startDerivative": vector(-6.86, 15.02) * mm, "endDerivative": vector(17.5, -8.04) * mm});
            skFitSpline(sketch, "E141", {"points": [v(-23.27, -64.98) * mm, v(-24.36, -61.57) * mm, v(-24.5, -58.16) * mm, v(-23.27, -56.6) * mm, v(-18.77, -58.98) * mm, v(-16.59, -60.82) * mm], "startDerivative": vector(-6, 16.08) * mm, "endDerivative": vector(9.6, -8.6) * mm});
            skFitSpline(sketch, "E142", {"points": [v(-16.59, -60.82) * mm, v(-17.02, -57) * mm, v(-16.2, -53.63) * mm], "startDerivative": vector(-1.5, 7.58) * mm, "endDerivative": vector(2.3, 6.8) * mm});
            skFitSpline(sketch, "E143", {"points": [v(-13.28, -53.63) * mm, v(-11.49, -55.25) * mm, v(-9.19, -58.16) * mm], "startDerivative": vector(3.98, -3.28) * mm, "endDerivative": vector(4.2, -5.7) * mm});
            skFitSpline(sketch, "E144", {"points": [v(-9.19, -58.16) * mm, v(-9.19, -55.6) * mm, v(-8.84, -53.63) * mm], "startDerivative": vector(-0.2, 4.99) * mm, "endDerivative": vector(0.92, 4.06) * mm});
            skFitSpline(sketch, "E145", {"points": [v(-3.34, -53.63) * mm, v(-2.52, -55.02) * mm, v(-1.9, -56.6) * mm], "startDerivative": vector(1.76, -2.75) * mm, "endDerivative": vector(1.13, -3.18) * mm});
            skFitSpline(sketch, "E146", {"points": [v(-1.9, -56.6) * mm, v(-1.43, -54.61) * mm, v(-0.93, -53.63) * mm], "startDerivative": vector(0.7, 3.76) * mm, "endDerivative": vector(1.27, 2.09) * mm});
            skFitSpline(sketch, "E147", {"points": [v(4.92, -53.63) * mm, v(5.78, -56.6) * mm, v(5.7, -56.6) * mm], "startDerivative": vector(1.67, -4.92) * mm, "endDerivative": vector(-0.68, 0.24) * mm});
            skFitSpline(sketch, "E148", {"points": [v(5.78, -56.6) * mm, v(6.75, -55.13) * mm, v(7.53, -53.63) * mm], "startDerivative": vector(2.02, 2.85) * mm, "endDerivative": vector(1.48, 3.08) * mm});
            skFitSpline(sketch, "E149", {"points": [v(12.63, -53.63) * mm, v(13.02, -55.13) * mm, v(13.41, -58.16) * mm], "startDerivative": vector(1, -3.3) * mm, "endDerivative": vector(0.6, -5.64) * mm});
            skFitSpline(sketch, "E150", {"points": [v(13.41, -58.16) * mm, v(15.36, -55.6) * mm, v(17.82, -53.63) * mm], "startDerivative": vector(3.61, 5.37) * mm, "endDerivative": vector(5.2, 3.7) * mm});
            skFitSpline(sketch, "E151", {"points": [v(20.43, -61.1) * mm, v(20.66, -57.24) * mm, v(19.8, -53.63) * mm], "startDerivative": vector(1.02, 7.73) * mm, "endDerivative": vector(-2.27, 7.22) * mm});
            skFitSpline(sketch, "E152", {"points": [v(20.35, -61.14) * mm, v(23.08, -58.98) * mm, v(25.92, -57.47) * mm, v(27.6, -58.16) * mm, v(27.95, -61.64) * mm, v(26.94, -65.46) * mm], "startDerivative": vector(12.56, 10.26) * mm, "endDerivative": vector(-5.5, -16.38) * mm});
            skFitSpline(sketch, "E153", {"points": [v(26.94, -65.46) * mm, v(30.17, -63.89) * mm, v(33.2, -62.85) * mm, v(34.38, -63.51) * mm, v(34.96, -64.98) * mm, v(33.29, -69.85) * mm], "startDerivative": vector(13.85, 6.75) * mm, "endDerivative": vector(-9.28, -20.46) * mm});
            skFitSpline(sketch, "E154", {"points": [v(-18.71, -69.85) * mm, v(-19.18, -67.12) * mm, v(-18.64, -64.98) * mm, v(-16.59, -64.98) * mm, v(-12.95, -67.74) * mm], "startDerivative": vector(-2.6, 10.81) * mm, "endDerivative": vector(11.5, -10.66) * mm});
            skFitSpline(sketch, "E155", {"points": [v(-12.95, -67.74) * mm, v(-12.95, -64.54) * mm, v(-12.52, -62.17) * mm, v(-11.74, -61.39) * mm, v(-10.3, -61.82) * mm, v(-7.02, -65.46) * mm], "startDerivative": vector(-0.36, 14.17) * mm, "endDerivative": vector(12.13, -15.63) * mm});
            skFitSpline(sketch, "E156", {"points": [v(-7.02, -65.46) * mm, v(-6.75, -62.64) * mm, v(-5.97, -60.44) * mm, v(-5.27, -59.6) * mm, v(-3.98, -59.83) * mm, v(-1.14, -64.17) * mm], "startDerivative": vector(0.52, 13.08) * mm, "endDerivative": vector(9.6, -18.53) * mm});
            skFitSpline(sketch, "E157", {"points": [v(-1.14, -64.17) * mm, v(-0.36, -62.01) * mm, v(1.08, -59.6) * mm, v(2.1, -58.98) * mm, v(3.3, -59.99) * mm, v(5.02, -64.54) * mm], "startDerivative": vector(3.33, 10.6) * mm, "endDerivative": vector(5.5, -18.4) * mm});
            skFitSpline(sketch, "E158", {"points": [v(5.02, -64.54) * mm, v(6.93, -61.47) * mm, v(8.76, -59.87) * mm, v(9.8, -60.44) * mm, v(10.9, -63.38) * mm, v(11.02, -65.8) * mm], "startDerivative": vector(7.39, 13.2) * mm, "endDerivative": vector(-0.3, -11.5) * mm});
            skFitSpline(sketch, "E159", {"points": [v(11.02, -65.8) * mm, v(12.8, -63.89) * mm, v(14.52, -62.25) * mm, v(16.04, -62.13) * mm, v(16.7, -62.9) * mm, v(16.75, -67.74) * mm], "startDerivative": vector(8.57, 8.72) * mm, "endDerivative": vector(-1.2, -20.16) * mm});
            skFitSpline(sketch, "E160", {"points": [v(16.75, -67.74) * mm, v(19.36, -66.22) * mm, v(21.54, -65.46) * mm, v(22.7, -66.34) * mm, v(22.43, -69.85) * mm], "startDerivative": vector(9.52, 5.7) * mm, "endDerivative": vector(-2.96, -13.65) * mm});
            skFitSpline(sketch, "E161", {"points": [v(46.98, -69.85) * mm, v(48.11, -67.74) * mm, v(47.84, -65.46) * mm, v(45.23, -64.54) * mm, v(38.57, -66.18) * mm], "startDerivative": vector(6.57, 9.38) * mm, "endDerivative": vector(-20.23, -6.73) * mm});
            skFitSpline(sketch, "E162", {"points": [v(38.57, -66.18) * mm, v(39.85, -63.38) * mm, v(41.18, -59.75) * mm, v(40.79, -56.6) * mm, v(38.57, -56.17) * mm, v(34.55, -57.57) * mm, v(31.9, -59.32) * mm], "startDerivative": vector(7.66, 16.88) * mm, "endDerivative": vector(-14.7, -11) * mm});
            skFitSpline(sketch, "E163", {"points": [v(31.9, -59.32) * mm, v(32.7, -56.6) * mm, v(32.7, -53.63) * mm], "startDerivative": vector(2.03, 5.43) * mm, "endDerivative": vector(-0.41, 5.96) * mm});
            skFitSpline(sketch, "E164", {"points": [v(47.1, -53.63) * mm, v(46.6, -56.13) * mm, v(44.41, -61.1) * mm], "startDerivative": vector(-0.75, -5.7) * mm, "endDerivative": vector(-4.4, -9.04) * mm});
            skFitSpline(sketch, "E165", {"points": [v(44.41, -61.1) * mm, v(48, -59.71) * mm, v(52.56, -58.98) * mm, v(54.93, -59.64) * mm, v(55.63, -60.82) * mm, v(54.97, -63.89) * mm, v(51, -69.85) * mm], "startDerivative": vector(19.47, 8.48) * mm, "endDerivative": vector(-19.9, -26.26) * mm});
            skFitSpline(sketch, "E166", {"points": [v(51.15, -53.63) * mm, v(50.3, -55.6) * mm], "startDerivative": vector(-0.86, -1.98) * mm, "endDerivative": vector(-0.86, -1.98) * mm});
            skFitSpline(sketch, "E167", {"points": [v(50.3, -55.6) * mm, v(52.56, -54.73) * mm, v(55.52, -53.63) * mm], "startDerivative": vector(4.67, 1.83) * mm, "endDerivative": vector(5.75, 2.11) * mm});
            skFitSpline(sketch, "E168", {"points": [v(61.67, -53.63) * mm, v(62.69, -54.53) * mm, v(62.69, -57.22) * mm, v(57.7, -66.18) * mm], "startDerivative": vector(6.02, -3.8) * mm, "endDerivative": vector(-12.08, -18.7) * mm});
            skFitSpline(sketch, "E169", {"points": [v(57.7, -66.18) * mm, v(62.1, -65.52) * mm, v(66.7, -65.48) * mm, v(69.2, -66.96) * mm, v(69.66, -68.75) * mm, v(69.2, -69.85) * mm], "startDerivative": vector(17.14, 2.82) * mm, "endDerivative": vector(-4.7, -7.7) * mm});
            skFitSpline(sketch, "E170", {"points": [v(64.25, -61.86) * mm, v(66.86, -58.27) * mm, v(69.08, -53.63) * mm], "startDerivative": vector(5.7, 7.08) * mm, "endDerivative": vector(3.99, 9.35) * mm});
            skFitSpline(sketch, "E171", {"points": [v(64.25, -61.86) * mm, v(67.99, -61.2) * mm, v(73.52, -60.8) * mm, v(76.56, -61.86) * mm, v(77.77, -62.95) * mm, v(77.42, -66.18) * mm, v(74.65, -69.85) * mm], "startDerivative": vector(20.11, 3.71) * mm, "endDerivative": vector(-17.2, -18.18) * mm});
            skFitSpline(sketch, "E172", {"points": [v(73.2, -53.63) * mm, v(72.04, -55.6) * mm, v(70.71, -57.6) * mm], "startDerivative": vector(-2.3, -4) * mm, "endDerivative": vector(-2.68, -3.96) * mm});
            skFitSpline(sketch, "E173", {"points": [v(70.71, -57.6) * mm, v(74.5, -56.75) * mm, v(80.34, -55.97) * mm, v(84.04, -56.67) * mm, v(85.6, -57.96) * mm, v(85.6, -60.38) * mm, v(84.08, -63.5) * mm, v(79.01, -69.85) * mm], "startDerivative": vector(24.93, 5.92) * mm, "endDerivative": vector(-28.52, -33.83) * mm});
            skFitSpline(sketch, "E174", {"points": [v(93.4, -53.63) * mm, v(93.31, -55.6) * mm, v(90.66, -61.08) * mm, v(84.27, -68.52) * mm], "startDerivative": vector(0.71, -8.78) * mm, "endDerivative": vector(-15.64, -16.43) * mm});
            skFitSpline(sketch, "E175", {"points": [v(84.27, -68.52) * mm, v(90.35, -68.2) * mm, v(95.1, -68.52) * mm, v(98.46, -69.85) * mm], "startDerivative": vector(16.46, 1.05) * mm, "endDerivative": vector(11, -5.4) * mm});
            skFitSpline(sketch, "E176", {"points": [v(148.88, 22.16) * mm, v(150.22, 23.01) * mm, v(153.05, 24.19) * mm, v(157, 23.47) * mm, v(159.26, 18.46) * mm, v(158.3, 3.66) * mm, v(150.8, -18.85) * mm], "startDerivative": vector(15.63, 10.33) * mm, "endDerivative": vector(-29.6, -76.06) * mm});
            skSolve(sketch);
        }
        {
            var Q0;
            Q0=qCreatedBy(makeId("Right.planeOp"),FACE);
            var sketch = newSketch(context, id + "F1", { "sketchPlane" : qUnion([Q0])});
            skLineSegment(sketch, "E177", {"start": v(0, 0) * mm, "end": v(0, 69.85) * mm});
            skLineSegment(sketch, "E178", {"start": v(0, 0) * mm, "end": v(0, -69.85) * mm});
            skLineSegment(sketch, "E179", {"start": v(0, -69.85) * mm, "end": v(12.13, 68.79) * mm});
            skLineSegment(sketch, "E180", {"start": v(12.13, 68.79) * mm, "end": v(0, 69.85) * mm});
            skSolve(sketch);
        }
        {
            var Q0;
            Q0=makeQuery(id+"F1.imprint","IMPRINT",FACE,{"disambiguationData":[TD([[makeQuery(id+"F1.imprint","IMPRINT",EDGE,{"derivedFrom":sQuery(id+"F1.wireOp",EDGE,"E177")}),-1.0]])]});
            extrude(context, id + "F2", {"entities" : qUnion([Q0]), "depth" : 165.1 * mm, "offsetDistance" : 25.4 * mm, "hasSecondDirection" : true, "secondDirectionOppositeDirection" : true, "secondDirectionDepth" : 165.1 * mm});
        }
        {
            var Q0;
            Q0=makeQuery(id+"F2.opExtrude","SWEPT_FACE",FACE,{"disambiguationData":[OSD([sQuery(id+"F1.wireOp",EDGE,"E179")])]});
            var sketch = newSketch(context, id + "F3", { "sketchPlane" : qUnion([Q0])});
            skLineSegment(sketch, "E181", {"start": v(-165.1, 69.58) * mm, "end": v(-165.1, -69.58) * mm});
            skLineSegment(sketch, "E182", {"start": v(-165.1, -69.58) * mm, "end": v(165.1, -69.58) * mm});
            skLineSegment(sketch, "E183", {"start": v(165.1, -69.58) * mm, "end": v(165.1, 69.58) * mm});
            skLineSegment(sketch, "E184", {"start": v(165.1, 69.58) * mm, "end": v(-165.1, 69.58) * mm});
            skSolve(sketch);
        }
        {
            var Q0;
            Q0 = qSketchRegion(id + "F3", true);
            extrude(context, id + "F4", {"entities" : qUnion([Q0]), "operationType" : NewBodyOperationType.ADD, "depth" : 25.4 * mm, "offsetDistance" : 25.4 * mm});
        }
        {
            var Q0;
            Q0=makeQuery(id+"F0.imprint","IMPRINT",FACE,{"disambiguationData":[TD([[makeQuery(id+"F0.imprint","IMPRINT",EDGE,{"derivedFrom":sQuery(id+"F0.wireOp",EDGE,"E0.bottom")}),1.0]])]});
            var Q1;
            Q1=makeQuery(id+"F0.imprint","IMPRINT",FACE,{"disambiguationData":[TD([[makeQuery(id+"F0.imprint","IMPRINT",EDGE,{"derivedFrom":sQuery(id+"F0.wireOp",EDGE,"E0.bottom")}),-1.0]])]});
            extrude(context, id + "F5", {"entities" : qUnion([Q0, Q1]), "operationType" : NewBodyOperationType.REMOVE, "endBound" : BoundingType.THROUGH_ALL, "oppositeDirection" : true, "depth" : 25.4 * mm, "offsetDistance" : 25.4 * mm});
        }
        {
            var Q0;
            Q0=makeQuery(id+"F0.imprint","IMPRINT",FACE,{"disambiguationData":[TD([[makeQuery(id+"F0.imprint","IMPRINT",EDGE,{"derivedFrom":sQuery(id+"F0.wireOp",EDGE,"E0.bottom")}),1.0]])]});
            extrude(context, id + "F6", {"entities" : qUnion([Q0]), "oppositeDirection" : true, "depth" : 7.62 * mm, "offsetDistance" : 25.4 * mm, "hasSecondDirection" : true, "secondDirectionOppositeDirection" : false, "secondDirectionDepth" : 2.54 * mm});
        }
        {
            var Q0;
            Q0=makeQuery(id+"F4.opExtrude","CAP_FACE",FACE,{"disambiguationData":[OSD([sQuery(id+"F3.wireOp",EDGE,"E181"),sQuery(id+"F3.wireOp",EDGE,"E182"),sQuery(id+"F3.wireOp",EDGE,"E183"),sQuery(id+"F3.wireOp",EDGE,"E184")])],"isStart":false});
            var sketch = newSketch(context, id + "F7", { "sketchPlane" : qUnion([Q0])});
            skLineSegment(sketch, "E185", {"start": v(-165.1, 69.58) * mm, "end": v(-165.1, -69.58) * mm});
            skLineSegment(sketch, "E186", {"start": v(-165.1, -69.58) * mm, "end": v(165.1, -69.58) * mm});
            skLineSegment(sketch, "E187", {"start": v(165.1, -69.58) * mm, "end": v(165.1, 69.58) * mm});
            skLineSegment(sketch, "E188", {"start": v(165.1, 69.58) * mm, "end": v(-165.1, 69.58) * mm});
            skLineSegment(sketch, "E189", {"start": v(-148.88, 56.58) * mm, "end": v(-148.88, -51.08) * mm});
            skLineSegment(sketch, "E190", {"start": v(-148.88, -51.08) * mm, "end": v(148.88, -51.08) * mm});
            skLineSegment(sketch, "E191", {"start": v(148.88, -51.08) * mm, "end": v(148.88, 56.58) * mm});
            skLineSegment(sketch, "E192", {"start": v(148.88, 56.58) * mm, "end": v(-148.88, 56.58) * mm});
            skFitSpline(sketch, "E193", {"points": [v(-162.74, -47.81) * mm, v(-162.6, -48.65) * mm, v(-162.25, -49.54) * mm, v(-161.86, -50.48) * mm, v(-161.11, -51.5) * mm, v(-160.7, -52.04) * mm, v(-159.57, -52.95) * mm, v(-158.88, -53.59) * mm, v(-158.23, -54.3) * mm, v(-158.26, -54.3) * mm], "startDerivative": vector(0.78, -7.44) * mm, "endDerivative": vector(-2.19, 0.56) * mm});
            skFitSpline(sketch, "E194", {"points": [v(-158.23, -54.3) * mm, v(-157.96, -53.6) * mm, v(-157.84, -53.2) * mm, v(-158.03, -52.45) * mm, v(-158.58, -51.69) * mm, v(-159.3, -51.01) * mm, v(-159.96, -50.58) * mm, v(-160.8, -50.03) * mm, v(-161.33, -49.68) * mm, v(-161.82, -49.27) * mm, v(-162.2, -48.67) * mm, v(-162.74, -47.81) * mm], "startDerivative": vector(3.1, 8.47) * mm, "endDerivative": vector(-5.7, 8.43) * mm});
            skFitSpline(sketch, "E195", {"points": [v(-163.06, -48.36) * mm, v(-163.18, -49.6) * mm, v(-163.22, -50.64) * mm, v(-163.17, -51.97) * mm, v(-162.71, -53.07) * mm, v(-162.07, -53.82) * mm, v(-161.11, -54.3) * mm, v(-160.1, -54.78) * mm, v(-159.3, -55.13) * mm, v(-158.87, -55.45) * mm], "startDerivative": vector(-1.22, -10.4) * mm, "endDerivative": vector(4.76, -4.19) * mm});
            skFitSpline(sketch, "E196", {"points": [v(-158.87, -55.45) * mm, v(-158.58, -55.08) * mm, v(-158.42, -54.7) * mm], "startDerivative": vector(0.6, 0.7) * mm, "endDerivative": vector(0.28, 0.79) * mm});
            skFitSpline(sketch, "E197", {"points": [v(-158.42, -54.7) * mm, v(-158.87, -54.1) * mm, v(-159.59, -53.46) * mm, v(-160.6, -52.61) * mm, v(-161.34, -51.9) * mm, v(-162.2, -50.56) * mm, v(-162.61, -49.7) * mm, v(-163.06, -48.36) * mm], "startDerivative": vector(-3.5, 5.27) * mm, "endDerivative": vector(-2.9, 8.97) * mm});
            skFitSpline(sketch, "E198", {"points": [v(-157.4, -53.05) * mm, v(-157.22, -52.79) * mm, v(-156.76, -52.42) * mm, v(-155.87, -51.98) * mm, v(-154.45, -51.25) * mm], "startDerivative": vector(0.97, 1.66) * mm, "endDerivative": vector(4.22, 2.2) * mm});
            skFitSpline(sketch, "E199", {"points": [v(-154.45, -51.25) * mm, v(-154.1, -51.47) * mm, v(-153.36, -51.8) * mm, v(-152.61, -52.08) * mm, v(-152.1, -52.22) * mm, v(-151.39, -52.51) * mm, v(-150.43, -53.1) * mm], "startDerivative": vector(2.44, -1.68) * mm, "endDerivative": vector(4.69, -3.09) * mm});
            skFitSpline(sketch, "E200", {"points": [v(-150.43, -53.1) * mm, v(-151, -53.05) * mm, v(-151.77, -52.99) * mm, v(-152.89, -53.05) * mm, v(-153.73, -53.18) * mm, v(-154.13, -53.32) * mm, v(-154.84, -53.5) * mm, v(-155.37, -53.59) * mm, v(-155.95, -53.59) * mm, v(-156.51, -53.53) * mm, v(-157.1, -53.34) * mm, v(-157.4, -53.05) * mm], "startDerivative": vector(-6.44, 0.5) * mm, "endDerivative": vector(-3.61, 4.19) * mm});
            skFitSpline(sketch, "E201", {"points": [v(-158.97, -61.4) * mm, v(-159.23, -61.06) * mm, v(-159.56, -60.82) * mm, v(-160.02, -59.91) * mm, v(-160.2, -59.33) * mm, v(-160.17, -58.6) * mm, v(-159.85, -57.89) * mm, v(-159.28, -57.33) * mm, v(-158.66, -56.8) * mm, v(-158.42, -56.22) * mm, v(-158.15, -55.45) * mm, v(-157.82, -54.62) * mm, v(-157.52, -54.2) * mm, v(-156.97, -54) * mm, v(-156.34, -53.97) * mm, v(-156.01, -54) * mm, v(-155.43, -54) * mm, v(-154.84, -53.94) * mm, v(-154.16, -53.92) * mm, v(-153.43, -53.71) * mm, v(-153.12, -53.5) * mm, v(-152.61, -53.46) * mm, v(-152.2, -53.73) * mm, v(-151.74, -54.06) * mm, v(-150.73, -55.25) * mm], "startDerivative": vector(-7.17, 11.17) * mm, "endDerivative": vector(16.74, -21.93) * mm});
            skFitSpline(sketch, "E202", {"points": [v(-150.73, -55.25) * mm, v(-151.6, -55.06) * mm, v(-152.4, -54.96) * mm, v(-153.03, -54.97) * mm, v(-153.74, -55.12) * mm, v(-154.24, -55.32) * mm, v(-154.93, -55.65) * mm, v(-155.79, -56.2) * mm, v(-156.37, -56.64) * mm, v(-157.01, -57.27) * mm, v(-157.88, -58.34) * mm, v(-158.42, -59.26) * mm, v(-158.74, -59.95) * mm, v(-158.88, -60.58) * mm, v(-158.97, -61.4) * mm], "startDerivative": vector(-11.72, 2.78) * mm, "endDerivative": vector(-1.14, -11.81) * mm});
            skFitSpline(sketch, "E203", {"points": [v(-162.14, -55.84) * mm, v(-161.13, -55.4) * mm, v(-160.59, -55.19) * mm, v(-160.21, -55.19) * mm, v(-159.6, -55.46) * mm, v(-159.05, -55.77) * mm], "startDerivative": vector(4.17, 1.71) * mm, "endDerivative": vector(2.71, -1.56) * mm});
            skFitSpline(sketch, "E204", {"points": [v(-159.05, -55.77) * mm, v(-159.02, -55.84) * mm, v(-159, -56.1) * mm, v(-159.22, -56.48) * mm, v(-159.75, -57.04) * mm, v(-160.2, -57.52) * mm, v(-160.54, -58.04) * mm, v(-160.69, -58.54) * mm, v(-160.73, -59.2) * mm, v(-160.63, -59.77) * mm, v(-160.52, -60.43) * mm], "startDerivative": vector(0.92, -1.43) * mm, "endDerivative": vector(0.95, -5.9) * mm});
            skFitSpline(sketch, "E205", {"points": [v(-160.52, -60.43) * mm, v(-160.82, -60.36) * mm, v(-161.13, -60.22) * mm, v(-161.44, -59.86) * mm, v(-161.64, -59.4) * mm, v(-161.77, -58.6) * mm, v(-161.81, -57.81) * mm, v(-161.86, -56.93) * mm, v(-161.96, -56.37) * mm, v(-162.14, -55.84) * mm], "startDerivative": vector(-3.66, 0.74) * mm, "endDerivative": vector(-1.78, 4.87) * mm});
            skFitSpline(sketch, "E206", {"points": [v(-161.74, -61.37) * mm, v(-161.38, -61.14) * mm, v(-160.6, -60.95) * mm, v(-159.77, -61.17) * mm, v(-159.28, -61.69) * mm, v(-159.02, -62.32) * mm, v(-158.79, -62.97) * mm, v(-158.43, -63.6) * mm, v(-157.45, -64.58) * mm, v(-156.42, -65.37) * mm, v(-155.42, -65.95) * mm, v(-154.5, -66.3) * mm, v(-153.75, -66.47) * mm, v(-152.43, -66.56) * mm], "startDerivative": vector(5.99, 4.47) * mm, "endDerivative": vector(15.19, -0.65) * mm});
            skFitSpline(sketch, "E207", {"points": [v(-152.43, -66.56) * mm, v(-152.78, -66.94) * mm, v(-153.5, -67.62) * mm, v(-154.26, -68.07) * mm, v(-154.91, -68.14) * mm, v(-155.7, -67.9) * mm, v(-156.5, -67.42) * mm, v(-157.05, -67.17) * mm, v(-157.65, -67) * mm, v(-158.84, -66.73) * mm, v(-159.47, -66.32) * mm, v(-159.85, -65.7) * mm, v(-160.1, -64.33) * mm, v(-160.2, -63.26) * mm, v(-160.64, -62.34) * mm, v(-161.74, -61.37) * mm], "startDerivative": vector(-6.28, -6.8) * mm, "endDerivative": vector(-14.4, 10.87) * mm});
            skFitSpline(sketch, "E208", {"points": [v(-152.56, -68.15) * mm, v(-152.54, -67.7) * mm, v(-152.18, -66.86) * mm, v(-151.77, -66.67) * mm, v(-151.23, -66.45) * mm, v(-150.36, -65.82) * mm, v(-149.57, -65.28) * mm, v(-148.82, -64.8) * mm, v(-147.81, -64.39) * mm, v(-147.07, -63.9) * mm, v(-146.59, -63.26) * mm, v(-146.03, -62.23) * mm, v(-145.83, -61.62) * mm], "startDerivative": vector(-0.38, 6.34) * mm, "endDerivative": vector(1.98, 7.6) * mm});
            skFitSpline(sketch, "E209", {"points": [v(-145.83, -61.62) * mm, v(-145.47, -61.9) * mm, v(-145.2, -62.32) * mm, v(-145.05, -62.62) * mm, v(-145.07, -63.64) * mm, v(-145.3, -64.5) * mm, v(-145.76, -65.1) * mm, v(-146.31, -65.55) * mm, v(-147.14, -65.95) * mm, v(-148.07, -66.2) * mm, v(-148.5, -66.34) * mm, v(-148.96, -66.7) * mm, v(-149.38, -67.3) * mm, v(-149.65, -67.67) * mm, v(-150.04, -67.98) * mm, v(-150.39, -68.1) * mm, v(-150.56, -68.13) * mm, v(-150.95, -68) * mm, v(-151.38, -67.85) * mm, v(-151.63, -67.77) * mm, v(-151.97, -67.8) * mm, v(-152.27, -67.95) * mm, v(-152.56, -68.15) * mm], "startDerivative": vector(9.08, -5.42) * mm, "endDerivative": vector(-7.75, -5.6) * mm});
            skFitSpline(sketch, "E210", {"points": [v(-145.86, -61.2) * mm, v(-145.84, -60.4) * mm, v(-145.73, -59.4) * mm, v(-145.68, -58.9) * mm, v(-145.8, -58.35) * mm, v(-146.2, -57.63) * mm, v(-146.45, -57.23) * mm, v(-146.7, -56.7) * mm, v(-146.96, -55.37) * mm, v(-147.3, -54.37) * mm], "startDerivative": vector(0, 6.61) * mm, "endDerivative": vector(-2.86, 7.07) * mm});
            skFitSpline(sketch, "E211", {"points": [v(-147.3, -54.37) * mm, v(-146.61, -54.52) * mm, v(-145.74, -54.87) * mm, v(-145.02, -55.39) * mm], "startDerivative": vector(2.19, -0.36) * mm, "endDerivative": vector(2, -1.6) * mm});
            skFitSpline(sketch, "E212", {"points": [v(-145.02, -55.39) * mm, v(-145.2, -55.72) * mm, v(-145.3, -56.13) * mm, v(-145.18, -56.84) * mm, v(-144.72, -57.9) * mm, v(-144.22, -58.94) * mm, v(-144, -59.61) * mm, v(-144.1, -60.16) * mm, v(-144.8, -60.79) * mm, v(-145.86, -61.2) * mm], "startDerivative": vector(-2.4, -4.23) * mm, "endDerivative": vector(-8.05, -2.56) * mm});
            skFitSpline(sketch, "E213", {"points": [v(-151.56, -53.65) * mm, v(-151.03, -53.68) * mm, v(-149.94, -53.54) * mm, v(-149.25, -53.43) * mm, v(-148.5, -53.6) * mm, v(-147.97, -54.14) * mm, v(-147.5, -55.2) * mm, v(-147.09, -57.29) * mm, v(-146.8, -58) * mm, v(-146.17, -58.94) * mm, v(-146.22, -59.7) * mm, v(-146.3, -61.02) * mm, v(-146.57, -61.51) * mm, v(-146.88, -62.8) * mm, v(-147.35, -63.54) * mm, v(-148.19, -64.12) * mm, v(-148.2, -64.1) * mm], "startDerivative": vector(9.53, -1.28) * mm, "endDerivative": vector(-0.77, 2.43) * mm});
            skFitSpline(sketch, "E214", {"points": [v(-148.19, -64.12) * mm, v(-147.8, -62.95) * mm, v(-147.64, -61.8) * mm, v(-147.5, -60.8) * mm, v(-147.42, -59.76) * mm, v(-147.85, -58.88) * mm, v(-148.47, -57.73) * mm, v(-149.64, -55.74) * mm, v(-150.84, -54.34) * mm, v(-151.56, -53.65) * mm], "startDerivative": vector(4.13, 10.67) * mm, "endDerivative": vector(-7, 6.49) * mm});
            skFitSpline(sketch, "E215", {"points": [v(-148.34, -59.6) * mm, v(-148.19, -59.8) * mm, v(-148.1, -60.48) * mm, v(-148.19, -61.71) * mm, v(-148.39, -63.1) * mm, v(-148.75, -64.32) * mm], "startDerivative": vector(1.6, -1.56) * mm, "endDerivative": vector(-1.7, -5.06) * mm});
            skFitSpline(sketch, "E216", {"points": [v(-148.75, -64.32) * mm, v(-149.22, -64.54) * mm, v(-149.78, -64.9) * mm, v(-150.84, -65.62) * mm, v(-151.08, -65.82) * mm, v(-152.04, -66.14) * mm, v(-153.37, -66.09) * mm, v(-154.06, -65.97) * mm, v(-155.12, -65.6) * mm, v(-156.15, -65.01) * mm, v(-157.23, -64.22) * mm, v(-158.09, -63.32) * mm, v(-158.38, -62.44) * mm, v(-158.44, -61.3) * mm, v(-158.26, -60.3) * mm, v(-157.7, -59.24) * mm, v(-156.77, -58) * mm], "startDerivative": vector(-10.6, -4.77) * mm, "endDerivative": vector(12.53, 16.13) * mm});
            skFitSpline(sketch, "E217", {"points": [v(-156.77, -58) * mm, v(-156.82, -58.93) * mm, v(-156.74, -59.92) * mm, v(-156.67, -61) * mm, v(-156.59, -62.04) * mm, v(-156.48, -62.3) * mm, v(-156.15, -62.4) * mm, v(-155.52, -62.65) * mm, v(-154.72, -63.22) * mm, v(-154.2, -63.6) * mm, v(-153.72, -64.02) * mm, v(-153.43, -64.32) * mm, v(-153.1, -64.52) * mm, v(-152.64, -64.56) * mm, v(-152, -64.4) * mm, v(-151.08, -63.92) * mm, v(-150.37, -63.39) * mm, v(-149.68, -62.6) * mm, v(-149.14, -61.55) * mm, v(-148.88, -60.8) * mm, v(-148.75, -60.17) * mm, v(-148.34, -59.6) * mm], "startDerivative": vector(-1.45, -17.2) * mm, "endDerivative": vector(10.51, 11.8) * mm});
            skFitSpline(sketch, "E218", {"points": [v(-149.61, -60.57) * mm, v(-149.24, -60.16) * mm, v(-148.92, -59.6) * mm, v(-148.75, -58.77) * mm, v(-148.75, -58.15) * mm, v(-149.09, -57.49) * mm, v(-149.9, -56.18) * mm, v(-150.17, -55.78) * mm, v(-150.4, -55.67) * mm, v(-150.7, -55.7) * mm, v(-151.26, -55.57) * mm, v(-152.16, -55.5) * mm, v(-152.96, -55.58) * mm, v(-153.6, -55.92) * mm, v(-154.01, -56.12) * mm, v(-154.9, -56.35) * mm, v(-155.74, -56.87) * mm, v(-156.13, -57.83) * mm, v(-156.35, -59.03) * mm, v(-156.15, -59.72) * mm, v(-155.7, -60.17) * mm, v(-154.87, -60.37) * mm], "startDerivative": vector(9.26, 9.51) * mm, "endDerivative": vector(17.6, -2.39) * mm});
            skFitSpline(sketch, "E219", {"points": [v(-154.87, -60.37) * mm, v(-154.87, -59.5) * mm, v(-154.58, -58.65) * mm, v(-154.05, -58) * mm, v(-153.2, -57.5) * mm, v(-152.04, -57.35) * mm, v(-151, -57.45) * mm, v(-150.2, -57.74) * mm, v(-149.7, -58.18) * mm, v(-149.48, -58.7) * mm, v(-149.46, -59.67) * mm, v(-149.61, -60.57) * mm], "startDerivative": vector(-0.68, 9.54) * mm, "endDerivative": vector(-1.97, -9.4) * mm});
            skFitSpline(sketch, "E220", {"points": [v(-152.93, -61.57) * mm, v(-153.25, -61.24) * mm, v(-153.44, -60.57) * mm, v(-153.46, -59.88) * mm, v(-153.13, -59.29) * mm, v(-152.24, -58.96) * mm, v(-151.7, -58.92) * mm, v(-151.28, -59.11) * mm, v(-151, -59.75) * mm, v(-151.02, -60.89) * mm, v(-151.26, -61.55) * mm, v(-151.78, -61.94) * mm, v(-152.54, -62.07) * mm, v(-153.46, -61.92) * mm, v(-154.36, -61.57) * mm, v(-155.24, -61.11) * mm, v(-156.15, -60.57) * mm], "startDerivative": vector(-7.39, 5.64) * mm, "endDerivative": vector(-12.38, 7.5) * mm});
            skFitSpline(sketch, "E221", {"points": [v(-152.93, -61.57) * mm, v(-153.5, -61.48) * mm, v(-153.96, -61.2) * mm, v(-154.22, -60.57) * mm, v(-154.35, -59.73) * mm, v(-154.32, -59.01) * mm, v(-154.1, -58.65) * mm, v(-153.43, -58.34) * mm, v(-152.7, -58) * mm, v(-152.34, -57.9) * mm, v(-151.7, -57.9) * mm, v(-150.76, -58.12) * mm, v(-150.3, -58.35) * mm, v(-150, -58.94) * mm, v(-149.92, -59.77) * mm, v(-150.05, -60.44) * mm, v(-150.07, -61.48) * mm, v(-149.94, -61.67) * mm, v(-149.8, -61.66) * mm, v(-149.8, -61.65) * mm], "startDerivative": vector(-10.92, 0.97) * mm, "endDerivative": vector(-0.64, 1.43) * mm});
            skFitSpline(sketch, "E222", {"points": [v(-149.8, -61.65) * mm, v(-149.94, -62.02) * mm, v(-150.52, -62.58) * mm, v(-151.4, -63.3) * mm, v(-152.44, -63.92) * mm, v(-152.93, -63.81) * mm, v(-153.78, -63.38) * mm, v(-154.42, -62.9) * mm, v(-155.07, -62.4) * mm, v(-155.69, -62.02) * mm, v(-155.93, -61.48) * mm, v(-156.15, -60.57) * mm], "startDerivative": vector(-1.4, -5.56) * mm, "endDerivative": vector(-2.3, 9.62) * mm});
            skFitSpline(sketch, "E223", {"points": [v(-151.98, -61.33) * mm, v(-151.73, -61.12) * mm, v(-151.56, -60.57) * mm, v(-151.68, -59.76) * mm, v(-151.84, -59.47) * mm, v(-152.63, -59.6) * mm, v(-152.93, -59.85) * mm, v(-153.05, -60.57) * mm, v(-152.72, -61.15) * mm, v(-151.98, -61.33) * mm]});
            skSolve(sketch);
        }
        {
            var Q0;
            Q0=makeQuery(id+"F7.imprint","IMPRINT",FACE,{"disambiguationData":[TD([[makeQuery(id+"F7.imprint","IMPRINT",EDGE,{"derivedFrom":sQuery(id+"F7.wireOp",EDGE,"E206")}),-1.0]])]});
            var Q1;
            Q1=makeQuery(id+"F7.imprint","IMPRINT",FACE,{"disambiguationData":[TD([[makeQuery(id+"F7.imprint","IMPRINT",EDGE,{"derivedFrom":sQuery(id+"F7.wireOp",EDGE,"E208")}),-1.0]])]});
            var Q2;
            Q2=makeQuery(id+"F7.imprint","IMPRINT",FACE,{"disambiguationData":[TD([[makeQuery(id+"F7.imprint","IMPRINT",EDGE,{"derivedFrom":sQuery(id+"F7.wireOp",EDGE,"E215")}),-1.0]])]});
            var Q3;
            {var subQ0=sQuery(id+"F7.wireOp",EDGE,"E220");Q3=makeQuery(id+"F7.imprint","IMPRINT",FACE,{"disambiguationData":[TD([[makeQuery(id+"F7.imprint","IMPRINT",EDGE,{"derivedFrom":subQ0}),1.0]])]});}
            var Q4;
            Q4=makeQuery(id+"F7.imprint","IMPRINT",FACE,{"disambiguationData":[TD([[makeQuery(id+"F7.imprint","IMPRINT",EDGE,{"derivedFrom":sQuery(id+"F7.wireOp",EDGE,"E223")}),1.0]])]});
            var Q5;
            Q5=makeQuery(id+"F7.imprint","IMPRINT",FACE,{"disambiguationData":[TD([[makeQuery(id+"F7.imprint","IMPRINT",EDGE,{"derivedFrom":sQuery(id+"F7.wireOp",EDGE,"E218")}),1.0]])]});
            var Q6;
            {var subQ0=sQuery(id+"F7.wireOp",EDGE,"E214");Q6=makeQuery(id+"F7.imprint","IMPRINT",FACE,{"disambiguationData":[TD([[makeQuery(id+"F7.imprint","IMPRINT",EDGE,{"derivedFrom":subQ0}),-1.0]])]});}
            var Q7;
            Q7=makeQuery(id+"F7.imprint","IMPRINT",FACE,{"disambiguationData":[TD([[makeQuery(id+"F7.imprint","IMPRINT",EDGE,{"derivedFrom":sQuery(id+"F7.wireOp",EDGE,"E210")}),-1.0]])]});
            var Q8;
            Q8=makeQuery(id+"F7.imprint","IMPRINT",FACE,{"disambiguationData":[TD([[makeQuery(id+"F7.imprint","IMPRINT",EDGE,{"derivedFrom":sQuery(id+"F7.wireOp",EDGE,"E201")}),-1.0]])]});
            var Q9;
            Q9=makeQuery(id+"F7.imprint","IMPRINT",FACE,{"disambiguationData":[TD([[makeQuery(id+"F7.imprint","IMPRINT",EDGE,{"derivedFrom":sQuery(id+"F7.wireOp",EDGE,"E203")}),-1.0]])]});
            var Q10;
            Q10=makeQuery(id+"F7.imprint","IMPRINT",FACE,{"disambiguationData":[TD([[makeQuery(id+"F7.imprint","IMPRINT",EDGE,{"derivedFrom":sQuery(id+"F7.wireOp",EDGE,"E195")}),1.0]])]});
            var Q11;
            {var subQ0=sQuery(id+"F7.wireOp",EDGE,"E194");Q11=makeQuery(id+"F7.imprint","IMPRINT",FACE,{"disambiguationData":[TD([[makeQuery(id+"F7.imprint","IMPRINT",EDGE,{"derivedFrom":subQ0}),1.0]])]});}
            var Q12;
            Q12=makeQuery(id+"F7.imprint","IMPRINT",FACE,{"disambiguationData":[TD([[makeQuery(id+"F7.imprint","IMPRINT",EDGE,{"derivedFrom":sQuery(id+"F7.wireOp",EDGE,"E198")}),-1.0]])]});
            extrude(context, id + "F8", {"entities" : qUnion([Q0, Q1, Q2, Q3, Q4, Q5, Q6, Q7, Q8, Q9, Q10, Q11, Q12]), "operationType" : NewBodyOperationType.REMOVE, "oppositeDirection" : true, "depth" : 5.08 * mm, "offsetDistance" : 25.4 * mm});
        }
        {
            var Q0;
            {var subQ18=sQuery(id+"F0.wireOp",EDGE,"E140");Q0=makeQuery(id+"F0.imprint","IMPRINT",FACE,{"disambiguationData":[TD([[makeQuery(id+"F0.imprint","IMPRINT",EDGE,{"derivedFrom":subQ18}),-1.0]])]});}
            var Q1;
            {var subQ1=sQuery(id+"F0.wireOp",EDGE,"E135");Q1=makeQuery(id+"F0.imprint","IMPRINT",FACE,{"disambiguationData":[TD([[makeQuery(id+"F0.imprint","IMPRINT",EDGE,{"derivedFrom":subQ1}),-1.0]])]});}
            var Q2;
            {var subQ0=sQuery(id+"F0.wireOp",EDGE,"E130");Q2=makeQuery(id+"F0.imprint","IMPRINT",FACE,{"disambiguationData":[TD([[makeQuery(id+"F0.imprint","IMPRINT",EDGE,{"derivedFrom":subQ0}),-1.0]])]});}
            var Q3;
            {var subQ1=sQuery(id+"F0.wireOp",EDGE,"E126");Q3=makeQuery(id+"F0.imprint","IMPRINT",FACE,{"disambiguationData":[TD([[makeQuery(id+"F0.imprint","IMPRINT",EDGE,{"derivedFrom":subQ1}),-1.0]])]});}
            var Q4;
            {var subQ5=sQuery(id+"F0.wireOp",EDGE,"E123");Q4=makeQuery(id+"F0.imprint","IMPRINT",FACE,{"disambiguationData":[TD([[makeQuery(id+"F0.imprint","IMPRINT",EDGE,{"derivedFrom":subQ5}),-1.0]])]});}
            var Q5;
            {var subQ0=sQuery(id+"F0.wireOp",EDGE,"E121");Q5=makeQuery(id+"F0.imprint","IMPRINT",FACE,{"disambiguationData":[TD([[makeQuery(id+"F0.imprint","IMPRINT",EDGE,{"derivedFrom":subQ0}),-1.0]])]});}
            var Q6;
            {var subQ0=sQuery(id+"F0.wireOp",EDGE,"E119");Q6=makeQuery(id+"F0.imprint","IMPRINT",FACE,{"disambiguationData":[TD([[makeQuery(id+"F0.imprint","IMPRINT",EDGE,{"derivedFrom":subQ0}),1.0]])]});}
            var Q7;
            {var subQ3=sQuery(id+"F0.wireOp",EDGE,"E117");Q7=makeQuery(id+"F0.imprint","IMPRINT",FACE,{"disambiguationData":[TD([[makeQuery(id+"F0.imprint","IMPRINT",EDGE,{"derivedFrom":subQ3}),-1.0]])]});}
            var Q8;
            {var subQ1=sQuery(id+"F0.wireOp",EDGE,"E113");Q8=makeQuery(id+"F0.imprint","IMPRINT",FACE,{"disambiguationData":[TD([[makeQuery(id+"F0.imprint","IMPRINT",EDGE,{"derivedFrom":subQ1}),-1.0]])]});}
            var Q9;
            {var subQ5=sQuery(id+"F0.wireOp",EDGE,"E4");Q9=makeQuery(id+"F0.imprint","IMPRINT",FACE,{"disambiguationData":[TD([[makeQuery(id+"F0.imprint","IMPRINT",EDGE,{"derivedFrom":subQ5}),1.0]])]});}
            var Q10;
            {var subQ0=sQuery(id+"F0.wireOp",EDGE,"E5");Q10=makeQuery(id+"F0.imprint","IMPRINT",FACE,{"disambiguationData":[TD([[makeQuery(id+"F0.imprint","IMPRINT",EDGE,{"derivedFrom":subQ0}),1.0]])]});}
            var Q11;
            {var subQ0=sQuery(id+"F0.wireOp",EDGE,"E7");Q11=makeQuery(id+"F0.imprint","IMPRINT",FACE,{"disambiguationData":[TD([[makeQuery(id+"F0.imprint","IMPRINT",EDGE,{"derivedFrom":subQ0}),1.0]])]});}
            var Q12;
            {var subQ0=sQuery(id+"F0.wireOp",EDGE,"E9");Q12=makeQuery(id+"F0.imprint","IMPRINT",FACE,{"disambiguationData":[TD([[makeQuery(id+"F0.imprint","IMPRINT",EDGE,{"derivedFrom":subQ0}),-1.0]])]});}
            var Q13;
            {var subQ0=sQuery(id+"F0.wireOp",EDGE,"E12");Q13=makeQuery(id+"F0.imprint","IMPRINT",FACE,{"disambiguationData":[TD([[makeQuery(id+"F0.imprint","IMPRINT",EDGE,{"derivedFrom":subQ0}),1.0]])]});}
            var Q14;
            {var subQ0=sQuery(id+"F0.wireOp",EDGE,"E14");Q14=makeQuery(id+"F0.imprint","IMPRINT",FACE,{"disambiguationData":[TD([[makeQuery(id+"F0.imprint","IMPRINT",EDGE,{"derivedFrom":subQ0}),1.0]])]});}
            var Q15;
            {var subQ0=sQuery(id+"F0.wireOp",EDGE,"E16");Q15=makeQuery(id+"F0.imprint","IMPRINT",FACE,{"disambiguationData":[TD([[makeQuery(id+"F0.imprint","IMPRINT",EDGE,{"derivedFrom":subQ0}),1.0]])]});}
            var Q16;
            {var subQ0=sQuery(id+"F0.wireOp",EDGE,"E19");Q16=makeQuery(id+"F0.imprint","IMPRINT",FACE,{"disambiguationData":[TD([[makeQuery(id+"F0.imprint","IMPRINT",EDGE,{"derivedFrom":subQ0}),1.0]])]});}
            var Q17;
            {var subQ0=sQuery(id+"F0.wireOp",EDGE,"E21");Q17=makeQuery(id+"F0.imprint","IMPRINT",FACE,{"disambiguationData":[TD([[makeQuery(id+"F0.imprint","IMPRINT",EDGE,{"derivedFrom":subQ0}),1.0]])]});}
            var Q18;
            {var subQ0=sQuery(id+"F0.wireOp",EDGE,"E25");Q18=makeQuery(id+"F0.imprint","IMPRINT",FACE,{"disambiguationData":[TD([[makeQuery(id+"F0.imprint","IMPRINT",EDGE,{"derivedFrom":subQ0}),1.0]])]});}
            var Q19;
            {var subQ0=sQuery(id+"F0.wireOp",EDGE,"E27");Q19=makeQuery(id+"F0.imprint","IMPRINT",FACE,{"disambiguationData":[TD([[makeQuery(id+"F0.imprint","IMPRINT",EDGE,{"derivedFrom":subQ0}),1.0]])]});}
            var Q20;
            {var subQ0=sQuery(id+"F0.wireOp",EDGE,"E32");Q20=makeQuery(id+"F0.imprint","IMPRINT",FACE,{"disambiguationData":[TD([[makeQuery(id+"F0.imprint","IMPRINT",EDGE,{"derivedFrom":subQ0}),-1.0]])]});}
            var Q21;
            {var subQ0=sQuery(id+"F0.wireOp",EDGE,"E34");Q21=makeQuery(id+"F0.imprint","IMPRINT",FACE,{"disambiguationData":[TD([[makeQuery(id+"F0.imprint","IMPRINT",EDGE,{"derivedFrom":subQ0}),-1.0]])]});}
            var Q22;
            {var subQ0=sQuery(id+"F0.wireOp",EDGE,"E36");Q22=makeQuery(id+"F0.imprint","IMPRINT",FACE,{"disambiguationData":[TD([[makeQuery(id+"F0.imprint","IMPRINT",EDGE,{"derivedFrom":subQ0}),-1.0]])]});}
            var Q23;
            {var subQ0=sQuery(id+"F0.wireOp",EDGE,"E39");Q23=makeQuery(id+"F0.imprint","IMPRINT",FACE,{"disambiguationData":[TD([[makeQuery(id+"F0.imprint","IMPRINT",EDGE,{"derivedFrom":subQ0}),-1.0]])]});}
            var Q24;
            {var subQ5=sQuery(id+"F0.wireOp",EDGE,"E42");Q24=makeQuery(id+"F0.imprint","IMPRINT",FACE,{"disambiguationData":[TD([[makeQuery(id+"F0.imprint","IMPRINT",EDGE,{"derivedFrom":subQ5}),-1.0]])]});}
            var Q25;
            {var subQ0=sQuery(id+"F0.wireOp",EDGE,"E44");Q25=makeQuery(id+"F0.imprint","IMPRINT",FACE,{"disambiguationData":[TD([[makeQuery(id+"F0.imprint","IMPRINT",EDGE,{"derivedFrom":subQ0}),-1.0]])]});}
            var Q26;
            {var subQ0=sQuery(id+"F0.wireOp",EDGE,"E47");Q26=makeQuery(id+"F0.imprint","IMPRINT",FACE,{"disambiguationData":[TD([[makeQuery(id+"F0.imprint","IMPRINT",EDGE,{"derivedFrom":subQ0}),1.0]])]});}
            var Q27;
            {var subQ0=sQuery(id+"F0.wireOp",EDGE,"E51");Q27=makeQuery(id+"F0.imprint","IMPRINT",FACE,{"disambiguationData":[TD([[makeQuery(id+"F0.imprint","IMPRINT",EDGE,{"derivedFrom":subQ0}),-1.0]])]});}
            var Q28;
            {var subQ0=sQuery(id+"F0.wireOp",EDGE,"E50");Q28=makeQuery(id+"F0.imprint","IMPRINT",FACE,{"disambiguationData":[TD([[makeQuery(id+"F0.imprint","IMPRINT",EDGE,{"derivedFrom":subQ0}),1.0]])]});}
            var Q29;
            {var subQ0=sQuery(id+"F0.wireOp",EDGE,"E53");Q29=makeQuery(id+"F0.imprint","IMPRINT",FACE,{"disambiguationData":[TD([[makeQuery(id+"F0.imprint","IMPRINT",EDGE,{"derivedFrom":subQ0}),1.0]])]});}
            var Q30;
            {var subQ0=sQuery(id+"F0.wireOp",EDGE,"E55");Q30=makeQuery(id+"F0.imprint","IMPRINT",FACE,{"disambiguationData":[TD([[makeQuery(id+"F0.imprint","IMPRINT",EDGE,{"derivedFrom":subQ0}),-1.0]])]});}
            var Q31;
            {var subQ0=sQuery(id+"F0.wireOp",EDGE,"E57");Q31=makeQuery(id+"F0.imprint","IMPRINT",FACE,{"disambiguationData":[TD([[makeQuery(id+"F0.imprint","IMPRINT",EDGE,{"derivedFrom":subQ0}),-1.0]])]});}
            var Q32;
            {var subQ1=sQuery(id+"F0.wireOp",EDGE,"E59");Q32=makeQuery(id+"F0.imprint","IMPRINT",FACE,{"disambiguationData":[TD([[makeQuery(id+"F0.imprint","IMPRINT",EDGE,{"derivedFrom":subQ1}),1.0]])]});}
            var Q33;
            {var subQ0=sQuery(id+"F0.wireOp",EDGE,"E63");Q33=makeQuery(id+"F0.imprint","IMPRINT",FACE,{"disambiguationData":[TD([[makeQuery(id+"F0.imprint","IMPRINT",EDGE,{"derivedFrom":subQ0}),-1.0]])]});}
            var Q34;
            {var subQ0=sQuery(id+"F0.wireOp",EDGE,"E65");Q34=makeQuery(id+"F0.imprint","IMPRINT",FACE,{"disambiguationData":[TD([[makeQuery(id+"F0.imprint","IMPRINT",EDGE,{"derivedFrom":subQ0}),1.0]])]});}
            var Q35;
            {var subQ0=sQuery(id+"F0.wireOp",EDGE,"E67");Q35=makeQuery(id+"F0.imprint","IMPRINT",FACE,{"disambiguationData":[TD([[makeQuery(id+"F0.imprint","IMPRINT",EDGE,{"derivedFrom":subQ0}),1.0]])]});}
            var Q36;
            {var subQ0=sQuery(id+"F0.wireOp",EDGE,"E69");Q36=makeQuery(id+"F0.imprint","IMPRINT",FACE,{"disambiguationData":[TD([[makeQuery(id+"F0.imprint","IMPRINT",EDGE,{"derivedFrom":subQ0}),-1.0]])]});}
            var Q37;
            {var subQ0=sQuery(id+"F0.wireOp",EDGE,"E71");Q37=makeQuery(id+"F0.imprint","IMPRINT",FACE,{"disambiguationData":[TD([[makeQuery(id+"F0.imprint","IMPRINT",EDGE,{"derivedFrom":subQ0}),1.0]])]});}
            var Q38;
            {var subQ0=sQuery(id+"F0.wireOp",EDGE,"E74");Q38=makeQuery(id+"F0.imprint","IMPRINT",FACE,{"disambiguationData":[TD([[makeQuery(id+"F0.imprint","IMPRINT",EDGE,{"derivedFrom":subQ0}),1.0]])]});}
            var Q39;
            {var subQ0=sQuery(id+"F0.wireOp",EDGE,"E76");Q39=makeQuery(id+"F0.imprint","IMPRINT",FACE,{"disambiguationData":[TD([[makeQuery(id+"F0.imprint","IMPRINT",EDGE,{"derivedFrom":subQ0}),-1.0]])]});}
            var Q40;
            {var subQ0=sQuery(id+"F0.wireOp",EDGE,"E79");Q40=makeQuery(id+"F0.imprint","IMPRINT",FACE,{"disambiguationData":[TD([[makeQuery(id+"F0.imprint","IMPRINT",EDGE,{"derivedFrom":subQ0}),1.0]])]});}
            var Q41;
            {var subQ1=sQuery(id+"F0.wireOp",EDGE,"E81");Q41=makeQuery(id+"F0.imprint","IMPRINT",FACE,{"disambiguationData":[TD([[makeQuery(id+"F0.imprint","IMPRINT",EDGE,{"derivedFrom":subQ1}),1.0]])]});}
            var Q42;
            {var subQ0=sQuery(id+"F0.wireOp",EDGE,"E85");Q42=makeQuery(id+"F0.imprint","IMPRINT",FACE,{"disambiguationData":[TD([[makeQuery(id+"F0.imprint","IMPRINT",EDGE,{"derivedFrom":subQ0}),-1.0]])]});}
            var Q43;
            {var subQ0=sQuery(id+"F0.wireOp",EDGE,"E87");Q43=makeQuery(id+"F0.imprint","IMPRINT",FACE,{"disambiguationData":[TD([[makeQuery(id+"F0.imprint","IMPRINT",EDGE,{"derivedFrom":subQ0}),-1.0]])]});}
            var Q44;
            {var subQ0=sQuery(id+"F0.wireOp",EDGE,"E92");Q44=makeQuery(id+"F0.imprint","IMPRINT",FACE,{"disambiguationData":[TD([[makeQuery(id+"F0.imprint","IMPRINT",EDGE,{"derivedFrom":subQ0}),-1.0]])]});}
            var Q45;
            {var subQ0=sQuery(id+"F0.wireOp",EDGE,"E95");Q45=makeQuery(id+"F0.imprint","IMPRINT",FACE,{"disambiguationData":[TD([[makeQuery(id+"F0.imprint","IMPRINT",EDGE,{"derivedFrom":subQ0}),-1.0]])]});}
            var Q46;
            {var subQ0=sQuery(id+"F0.wireOp",EDGE,"E99");Q46=makeQuery(id+"F0.imprint","IMPRINT",FACE,{"disambiguationData":[TD([[makeQuery(id+"F0.imprint","IMPRINT",EDGE,{"derivedFrom":subQ0}),-1.0]])]});}
            var Q47;
            {var subQ1=sQuery(id+"F0.wireOp",EDGE,"E103");Q47=makeQuery(id+"F0.imprint","IMPRINT",FACE,{"disambiguationData":[TD([[makeQuery(id+"F0.imprint","IMPRINT",EDGE,{"derivedFrom":subQ1}),1.0]])]});}
            var Q48;
            {var subQ1=sQuery(id+"F0.wireOp",EDGE,"E106");Q48=makeQuery(id+"F0.imprint","IMPRINT",FACE,{"disambiguationData":[TD([[makeQuery(id+"F0.imprint","IMPRINT",EDGE,{"derivedFrom":subQ1}),-1.0]])]});}
            var Q49;
            {var subQ1=sQuery(id+"F0.wireOp",EDGE,"E109");Q49=makeQuery(id+"F0.imprint","IMPRINT",FACE,{"disambiguationData":[TD([[makeQuery(id+"F0.imprint","IMPRINT",EDGE,{"derivedFrom":subQ1}),1.0]])]});}
            var Q50;
            {var subQ1=sQuery(id+"F0.wireOp",EDGE,"E172");Q50=makeQuery(id+"F0.imprint","IMPRINT",FACE,{"disambiguationData":[TD([[makeQuery(id+"F0.imprint","IMPRINT",EDGE,{"derivedFrom":subQ1}),1.0]])]});}
            var Q51;
            {var subQ0=sQuery(id+"F0.wireOp",EDGE,"E168");Q51=makeQuery(id+"F0.imprint","IMPRINT",FACE,{"disambiguationData":[TD([[makeQuery(id+"F0.imprint","IMPRINT",EDGE,{"derivedFrom":subQ0}),1.0]])]});}
            var Q52;
            {var subQ0=sQuery(id+"F0.wireOp",EDGE,"E161");Q52=makeQuery(id+"F0.imprint","IMPRINT",FACE,{"disambiguationData":[TD([[makeQuery(id+"F0.imprint","IMPRINT",EDGE,{"derivedFrom":subQ0}),-1.0]])]});}
            var Q53;
            {var subQ0=sQuery(id+"F0.wireOp",EDGE,"E166");Q53=makeQuery(id+"F0.imprint","IMPRINT",FACE,{"disambiguationData":[TD([[makeQuery(id+"F0.imprint","IMPRINT",EDGE,{"derivedFrom":subQ0}),1.0]])]});}
            extrude(context, id + "F9", {"entities" : qUnion([Q0, Q1, Q2, Q3, Q4, Q5, Q6, Q7, Q8, Q9, Q10, Q11, Q12, Q13, Q14, Q15, Q16, Q17, Q18, Q19, Q20, Q21, Q22, Q23, Q24, Q25, Q26, Q27, Q28, Q29, Q30, Q31, Q32, Q33, Q34, Q35, Q36, Q37, Q38, Q39, Q40, Q41, Q42, Q43, Q44, Q45, Q46, Q47, Q48, Q49, Q50, Q51, Q52, Q53]), "depth" : 2.54 * mm, "offsetDistance" : 25.4 * mm});
        }
    });
